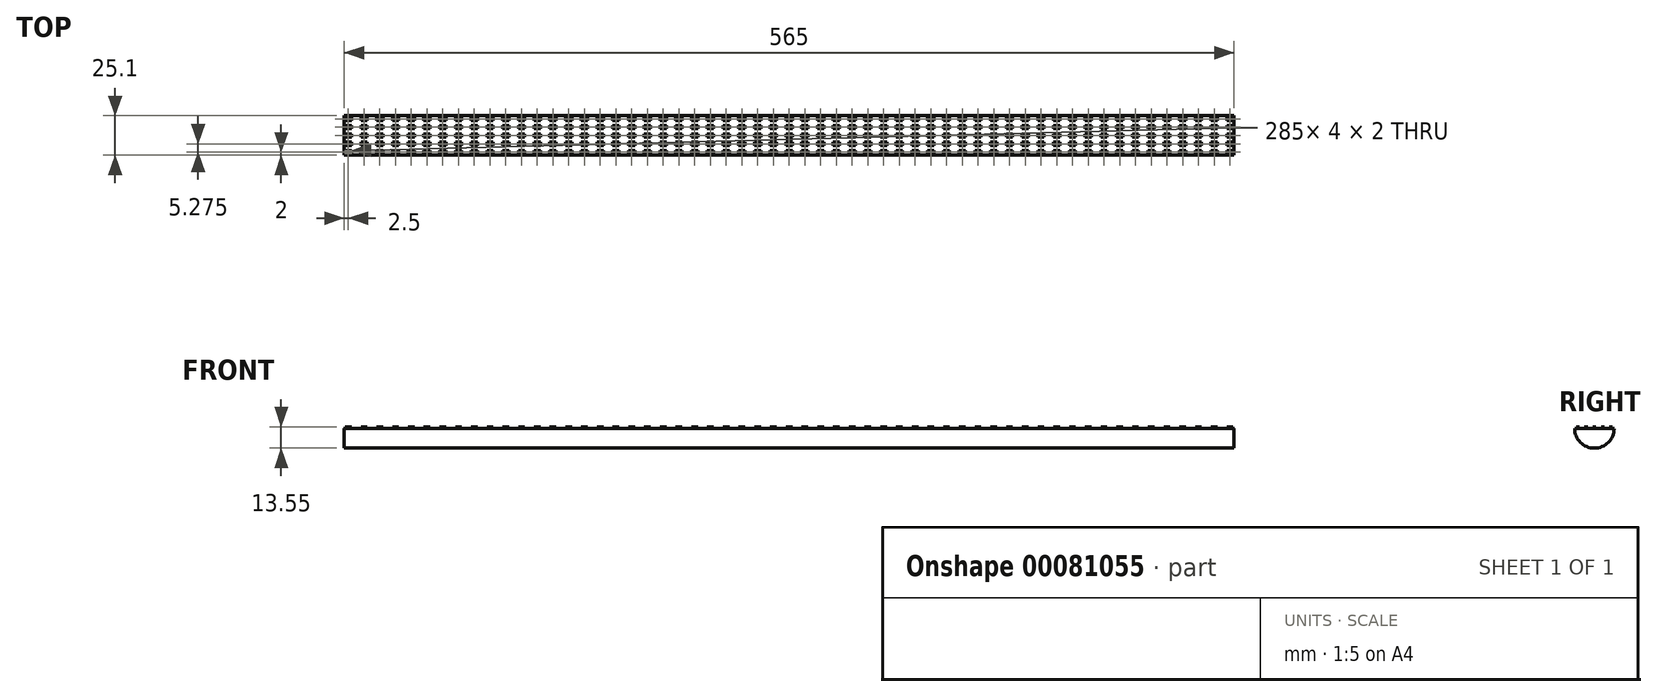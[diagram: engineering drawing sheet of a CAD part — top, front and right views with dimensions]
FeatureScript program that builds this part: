
annotation { "Feature Type Name" : "Feature", "Feature Type Description" : "" }
export const myFeature = defineFeature(function(context is Context, id is Id, definition is map)
    precondition{}
    {
        {
            var Q0;
            Q0=qCreatedBy(makeId("Right.planeOp"),FACE);
            var sketch = newSketch(context, id + "F0", { "sketchPlane" : qUnion([Q0])});
            skArc(sketch, "E0", {"start": v(-12.55, 0) * mm, "mid": v(0, -12.55) * mm, "end": v(12.55, 0) * mm});
            skLineSegment(sketch, "E1", {"start": v(-12.55, 0) * mm, "end": v(12.55, 0) * mm});
            skSolve(sketch);
        }
        {
            var Q0;
            Q0=qSketchRegion(id+"F0",true);
            extrude(context, id + "F1", {"entities" : qUnion([Q0]), "endBound" : BoundingType.SYMMETRIC, "depth" : 565 * mm});
        }
        {
            var Q0;
            Q0=makeQuery(id+"F1.opExtrude","SWEPT_FACE",FACE,{"disambiguationData":[OSD([sQuery(id+"F0.wireOp",EDGE,"E1")])]});
            var sketch = newSketch(context, id + "F2", { "sketchPlane" : qUnion([Q0])});
            skLineSegment(sketch, "E2.bottom", {"start": v(-282, 11.55) * mm, "end": v(-278, 11.55) * mm});
            skLineSegment(sketch, "E2.top", {"start": v(-282, 9.55) * mm, "end": v(-278, 9.55) * mm});
            skLineSegment(sketch, "E2.left", {"start": v(-282, 11.55) * mm, "end": v(-282, 9.55) * mm});
            skLineSegment(sketch, "E2.right", {"start": v(-278, 11.55) * mm, "end": v(-278, 9.55) * mm});
            skLineSegment(sketch, "E3.1.0.0", {"start": v(-282, 6.27) * mm, "end": v(-282, 4.27) * mm});
            skLineSegment(sketch, "E3.1.0.1", {"start": v(-282, 6.27) * mm, "end": v(-278, 6.27) * mm});
            skLineSegment(sketch, "E3.1.0.2", {"start": v(-278, 6.27) * mm, "end": v(-278, 4.27) * mm});
            skLineSegment(sketch, "E3.1.0.3", {"start": v(-282, 4.27) * mm, "end": v(-278, 4.27) * mm});
            skLineSegment(sketch, "E3.2.0.0", {"start": v(-282, 1) * mm, "end": v(-282, -1) * mm});
            skLineSegment(sketch, "E3.2.0.1", {"start": v(-282, 1) * mm, "end": v(-278, 1) * mm});
            skLineSegment(sketch, "E3.2.0.2", {"start": v(-278, 1) * mm, "end": v(-278, -1) * mm});
            skLineSegment(sketch, "E3.2.0.3", {"start": v(-282, -1) * mm, "end": v(-278, -1) * mm});
            skLineSegment(sketch, "E3.direction1", {"start": v(-278, 9.55) * mm, "end": v(-278, 4.27) * mm, "construction": true});
            skLineSegment(sketch, "E4.0.3.0", {"start": v(-282, -4.28) * mm, "end": v(-282, -6.28) * mm});
            skLineSegment(sketch, "E4.3.3.0", {"start": v(-282, -4.28) * mm, "end": v(-278, -4.28) * mm});
            skLineSegment(sketch, "E4.6.3.0", {"start": v(-278, -4.28) * mm, "end": v(-278, -6.28) * mm});
            skLineSegment(sketch, "E4.9.3.0", {"start": v(-282, -6.28) * mm, "end": v(-278, -6.28) * mm});
            skLineSegment(sketch, "E5.0.4.0", {"start": v(-282, -9.55) * mm, "end": v(-282, -11.55) * mm});
            skLineSegment(sketch, "E5.3.4.0", {"start": v(-282, -9.55) * mm, "end": v(-278, -9.55) * mm});
            skLineSegment(sketch, "E5.6.4.0", {"start": v(-278, -9.55) * mm, "end": v(-278, -11.55) * mm});
            skLineSegment(sketch, "E5.9.4.0", {"start": v(-282, -11.55) * mm, "end": v(-278, -11.55) * mm});
            skLineSegment(sketch, "E6.1.0.0", {"start": v(-272, -9.55) * mm, "end": v(-272, -11.55) * mm});
            skLineSegment(sketch, "E6.1.0.1", {"start": v(-268, -9.55) * mm, "end": v(-268, -11.55) * mm});
            skLineSegment(sketch, "E6.1.0.2", {"start": v(-272, -9.55) * mm, "end": v(-268, -9.55) * mm});
            skLineSegment(sketch, "E6.1.0.3", {"start": v(-268, 9.55) * mm, "end": v(-268, 4.27) * mm, "construction": true});
            skLineSegment(sketch, "E6.1.0.4", {"start": v(-272, -1) * mm, "end": v(-268, -1) * mm});
            skLineSegment(sketch, "E6.1.0.5", {"start": v(-272, -11.55) * mm, "end": v(-268, -11.55) * mm});
            skLineSegment(sketch, "E6.1.0.6", {"start": v(-268, 1) * mm, "end": v(-268, -1) * mm});
            skLineSegment(sketch, "E6.1.0.7", {"start": v(-272, 1) * mm, "end": v(-268, 1) * mm});
            skLineSegment(sketch, "E6.1.0.8", {"start": v(-272, 1) * mm, "end": v(-272, -1) * mm});
            skLineSegment(sketch, "E6.1.0.9", {"start": v(-272, 4.27) * mm, "end": v(-268, 4.27) * mm});
            skLineSegment(sketch, "E6.1.0.10", {"start": v(-268, 6.27) * mm, "end": v(-268, 4.27) * mm});
            skLineSegment(sketch, "E6.1.0.11", {"start": v(-272, 6.27) * mm, "end": v(-268, 6.27) * mm});
            skLineSegment(sketch, "E6.1.0.12", {"start": v(-272, 6.27) * mm, "end": v(-272, 4.27) * mm});
            skLineSegment(sketch, "E6.1.0.13", {"start": v(-268, 11.55) * mm, "end": v(-268, 9.55) * mm});
            skLineSegment(sketch, "E6.1.0.14", {"start": v(-272, 11.55) * mm, "end": v(-272, 9.55) * mm});
            skLineSegment(sketch, "E6.1.0.15", {"start": v(-272, 9.55) * mm, "end": v(-268, 9.55) * mm});
            skLineSegment(sketch, "E6.1.0.16", {"start": v(-272, -6.28) * mm, "end": v(-268, -6.28) * mm});
            skLineSegment(sketch, "E6.1.0.17", {"start": v(-272, 11.55) * mm, "end": v(-268, 11.55) * mm});
            skLineSegment(sketch, "E6.1.0.18", {"start": v(-268, -4.28) * mm, "end": v(-268, -6.28) * mm});
            skLineSegment(sketch, "E6.1.0.19", {"start": v(-272, -4.28) * mm, "end": v(-268, -4.28) * mm});
            skLineSegment(sketch, "E6.1.0.20", {"start": v(-272, -4.28) * mm, "end": v(-272, -6.28) * mm});
            skLineSegment(sketch, "E6.2.0.0", {"start": v(-262, -9.55) * mm, "end": v(-262, -11.55) * mm});
            skLineSegment(sketch, "E6.2.0.1", {"start": v(-258, -9.55) * mm, "end": v(-258, -11.55) * mm});
            skLineSegment(sketch, "E6.2.0.2", {"start": v(-262, -9.55) * mm, "end": v(-258, -9.55) * mm});
            skLineSegment(sketch, "E6.2.0.3", {"start": v(-258, 9.55) * mm, "end": v(-258, 4.27) * mm, "construction": true});
            skLineSegment(sketch, "E6.2.0.4", {"start": v(-262, -1) * mm, "end": v(-258, -1) * mm});
            skLineSegment(sketch, "E6.2.0.5", {"start": v(-262, -11.55) * mm, "end": v(-258, -11.55) * mm});
            skLineSegment(sketch, "E6.2.0.6", {"start": v(-258, 1) * mm, "end": v(-258, -1) * mm});
            skLineSegment(sketch, "E6.2.0.7", {"start": v(-262, 1) * mm, "end": v(-258, 1) * mm});
            skLineSegment(sketch, "E6.2.0.8", {"start": v(-262, 1) * mm, "end": v(-262, -1) * mm});
            skLineSegment(sketch, "E6.2.0.9", {"start": v(-262, 4.27) * mm, "end": v(-258, 4.27) * mm});
            skLineSegment(sketch, "E6.2.0.10", {"start": v(-258, 6.27) * mm, "end": v(-258, 4.27) * mm});
            skLineSegment(sketch, "E6.2.0.11", {"start": v(-262, 6.27) * mm, "end": v(-258, 6.27) * mm});
            skLineSegment(sketch, "E6.2.0.12", {"start": v(-262, 6.27) * mm, "end": v(-262, 4.27) * mm});
            skLineSegment(sketch, "E6.2.0.13", {"start": v(-258, 11.55) * mm, "end": v(-258, 9.55) * mm});
            skLineSegment(sketch, "E6.2.0.14", {"start": v(-262, 11.55) * mm, "end": v(-262, 9.55) * mm});
            skLineSegment(sketch, "E6.2.0.15", {"start": v(-262, 9.55) * mm, "end": v(-258, 9.55) * mm});
            skLineSegment(sketch, "E6.2.0.16", {"start": v(-262, -6.28) * mm, "end": v(-258, -6.28) * mm});
            skLineSegment(sketch, "E6.2.0.17", {"start": v(-262, 11.55) * mm, "end": v(-258, 11.55) * mm});
            skLineSegment(sketch, "E6.2.0.18", {"start": v(-258, -4.28) * mm, "end": v(-258, -6.28) * mm});
            skLineSegment(sketch, "E6.2.0.19", {"start": v(-262, -4.28) * mm, "end": v(-258, -4.28) * mm});
            skLineSegment(sketch, "E6.2.0.20", {"start": v(-262, -4.28) * mm, "end": v(-262, -6.28) * mm});
            skLineSegment(sketch, "E6.3.0.0", {"start": v(-252, -9.55) * mm, "end": v(-252, -11.55) * mm});
            skLineSegment(sketch, "E6.3.0.1", {"start": v(-248, -9.55) * mm, "end": v(-248, -11.55) * mm});
            skLineSegment(sketch, "E6.3.0.2", {"start": v(-252, -9.55) * mm, "end": v(-248, -9.55) * mm});
            skLineSegment(sketch, "E6.3.0.3", {"start": v(-248, 9.55) * mm, "end": v(-248, 4.27) * mm, "construction": true});
            skLineSegment(sketch, "E6.3.0.4", {"start": v(-252, -1) * mm, "end": v(-248, -1) * mm});
            skLineSegment(sketch, "E6.3.0.5", {"start": v(-252, -11.55) * mm, "end": v(-248, -11.55) * mm});
            skLineSegment(sketch, "E6.3.0.6", {"start": v(-248, 1) * mm, "end": v(-248, -1) * mm});
            skLineSegment(sketch, "E6.3.0.7", {"start": v(-252, 1) * mm, "end": v(-248, 1) * mm});
            skLineSegment(sketch, "E6.3.0.8", {"start": v(-252, 1) * mm, "end": v(-252, -1) * mm});
            skLineSegment(sketch, "E6.3.0.9", {"start": v(-252, 4.27) * mm, "end": v(-248, 4.27) * mm});
            skLineSegment(sketch, "E6.3.0.10", {"start": v(-248, 6.27) * mm, "end": v(-248, 4.27) * mm});
            skLineSegment(sketch, "E6.3.0.11", {"start": v(-252, 6.27) * mm, "end": v(-248, 6.27) * mm});
            skLineSegment(sketch, "E6.3.0.12", {"start": v(-252, 6.27) * mm, "end": v(-252, 4.27) * mm});
            skLineSegment(sketch, "E6.3.0.13", {"start": v(-248, 11.55) * mm, "end": v(-248, 9.55) * mm});
            skLineSegment(sketch, "E6.3.0.14", {"start": v(-252, 11.55) * mm, "end": v(-252, 9.55) * mm});
            skLineSegment(sketch, "E6.3.0.15", {"start": v(-252, 9.55) * mm, "end": v(-248, 9.55) * mm});
            skLineSegment(sketch, "E6.3.0.16", {"start": v(-252, -6.28) * mm, "end": v(-248, -6.28) * mm});
            skLineSegment(sketch, "E6.3.0.17", {"start": v(-252, 11.55) * mm, "end": v(-248, 11.55) * mm});
            skLineSegment(sketch, "E6.3.0.18", {"start": v(-248, -4.28) * mm, "end": v(-248, -6.28) * mm});
            skLineSegment(sketch, "E6.3.0.19", {"start": v(-252, -4.28) * mm, "end": v(-248, -4.28) * mm});
            skLineSegment(sketch, "E6.3.0.20", {"start": v(-252, -4.28) * mm, "end": v(-252, -6.28) * mm});
            skLineSegment(sketch, "E6.4.0.0", {"start": v(-242, -9.55) * mm, "end": v(-242, -11.55) * mm});
            skLineSegment(sketch, "E6.4.0.1", {"start": v(-238, -9.55) * mm, "end": v(-238, -11.55) * mm});
            skLineSegment(sketch, "E6.4.0.2", {"start": v(-242, -9.55) * mm, "end": v(-238, -9.55) * mm});
            skLineSegment(sketch, "E6.4.0.3", {"start": v(-238, 9.55) * mm, "end": v(-238, 4.27) * mm, "construction": true});
            skLineSegment(sketch, "E6.4.0.4", {"start": v(-242, -1) * mm, "end": v(-238, -1) * mm});
            skLineSegment(sketch, "E6.4.0.5", {"start": v(-242, -11.55) * mm, "end": v(-238, -11.55) * mm});
            skLineSegment(sketch, "E6.4.0.6", {"start": v(-238, 1) * mm, "end": v(-238, -1) * mm});
            skLineSegment(sketch, "E6.4.0.7", {"start": v(-242, 1) * mm, "end": v(-238, 1) * mm});
            skLineSegment(sketch, "E6.4.0.8", {"start": v(-242, 1) * mm, "end": v(-242, -1) * mm});
            skLineSegment(sketch, "E6.4.0.9", {"start": v(-242, 4.27) * mm, "end": v(-238, 4.27) * mm});
            skLineSegment(sketch, "E6.4.0.10", {"start": v(-238, 6.27) * mm, "end": v(-238, 4.27) * mm});
            skLineSegment(sketch, "E6.4.0.11", {"start": v(-242, 6.27) * mm, "end": v(-238, 6.27) * mm});
            skLineSegment(sketch, "E6.4.0.12", {"start": v(-242, 6.27) * mm, "end": v(-242, 4.27) * mm});
            skLineSegment(sketch, "E6.4.0.13", {"start": v(-238, 11.55) * mm, "end": v(-238, 9.55) * mm});
            skLineSegment(sketch, "E6.4.0.14", {"start": v(-242, 11.55) * mm, "end": v(-242, 9.55) * mm});
            skLineSegment(sketch, "E6.4.0.15", {"start": v(-242, 9.55) * mm, "end": v(-238, 9.55) * mm});
            skLineSegment(sketch, "E6.4.0.16", {"start": v(-242, -6.28) * mm, "end": v(-238, -6.28) * mm});
            skLineSegment(sketch, "E6.4.0.17", {"start": v(-242, 11.55) * mm, "end": v(-238, 11.55) * mm});
            skLineSegment(sketch, "E6.4.0.18", {"start": v(-238, -4.28) * mm, "end": v(-238, -6.28) * mm});
            skLineSegment(sketch, "E6.4.0.19", {"start": v(-242, -4.28) * mm, "end": v(-238, -4.28) * mm});
            skLineSegment(sketch, "E6.4.0.20", {"start": v(-242, -4.28) * mm, "end": v(-242, -6.28) * mm});
            skLineSegment(sketch, "E6.5.0.0", {"start": v(-232, -9.55) * mm, "end": v(-232, -11.55) * mm});
            skLineSegment(sketch, "E6.5.0.1", {"start": v(-228, -9.55) * mm, "end": v(-228, -11.55) * mm});
            skLineSegment(sketch, "E6.5.0.2", {"start": v(-232, -9.55) * mm, "end": v(-228, -9.55) * mm});
            skLineSegment(sketch, "E6.5.0.3", {"start": v(-228, 9.55) * mm, "end": v(-228, 4.27) * mm, "construction": true});
            skLineSegment(sketch, "E6.5.0.4", {"start": v(-232, -1) * mm, "end": v(-228, -1) * mm});
            skLineSegment(sketch, "E6.5.0.5", {"start": v(-232, -11.55) * mm, "end": v(-228, -11.55) * mm});
            skLineSegment(sketch, "E6.5.0.6", {"start": v(-228, 1) * mm, "end": v(-228, -1) * mm});
            skLineSegment(sketch, "E6.5.0.7", {"start": v(-232, 1) * mm, "end": v(-228, 1) * mm});
            skLineSegment(sketch, "E6.5.0.8", {"start": v(-232, 1) * mm, "end": v(-232, -1) * mm});
            skLineSegment(sketch, "E6.5.0.9", {"start": v(-232, 4.27) * mm, "end": v(-228, 4.27) * mm});
            skLineSegment(sketch, "E6.5.0.10", {"start": v(-228, 6.27) * mm, "end": v(-228, 4.27) * mm});
            skLineSegment(sketch, "E6.5.0.11", {"start": v(-232, 6.27) * mm, "end": v(-228, 6.27) * mm});
            skLineSegment(sketch, "E6.5.0.12", {"start": v(-232, 6.27) * mm, "end": v(-232, 4.27) * mm});
            skLineSegment(sketch, "E6.5.0.13", {"start": v(-228, 11.55) * mm, "end": v(-228, 9.55) * mm});
            skLineSegment(sketch, "E6.5.0.14", {"start": v(-232, 11.55) * mm, "end": v(-232, 9.55) * mm});
            skLineSegment(sketch, "E6.5.0.15", {"start": v(-232, 9.55) * mm, "end": v(-228, 9.55) * mm});
            skLineSegment(sketch, "E6.5.0.16", {"start": v(-232, -6.28) * mm, "end": v(-228, -6.28) * mm});
            skLineSegment(sketch, "E6.5.0.17", {"start": v(-232, 11.55) * mm, "end": v(-228, 11.55) * mm});
            skLineSegment(sketch, "E6.5.0.18", {"start": v(-228, -4.28) * mm, "end": v(-228, -6.28) * mm});
            skLineSegment(sketch, "E6.5.0.19", {"start": v(-232, -4.28) * mm, "end": v(-228, -4.28) * mm});
            skLineSegment(sketch, "E6.5.0.20", {"start": v(-232, -4.28) * mm, "end": v(-232, -6.28) * mm});
            skLineSegment(sketch, "E6.6.0.0", {"start": v(-222, -9.55) * mm, "end": v(-222, -11.55) * mm});
            skLineSegment(sketch, "E6.6.0.1", {"start": v(-218, -9.55) * mm, "end": v(-218, -11.55) * mm});
            skLineSegment(sketch, "E6.6.0.2", {"start": v(-222, -9.55) * mm, "end": v(-218, -9.55) * mm});
            skLineSegment(sketch, "E6.6.0.3", {"start": v(-218, 9.55) * mm, "end": v(-218, 4.27) * mm, "construction": true});
            skLineSegment(sketch, "E6.6.0.4", {"start": v(-222, -1) * mm, "end": v(-218, -1) * mm});
            skLineSegment(sketch, "E6.6.0.5", {"start": v(-222, -11.55) * mm, "end": v(-218, -11.55) * mm});
            skLineSegment(sketch, "E6.6.0.6", {"start": v(-218, 1) * mm, "end": v(-218, -1) * mm});
            skLineSegment(sketch, "E6.6.0.7", {"start": v(-222, 1) * mm, "end": v(-218, 1) * mm});
            skLineSegment(sketch, "E6.6.0.8", {"start": v(-222, 1) * mm, "end": v(-222, -1) * mm});
            skLineSegment(sketch, "E6.6.0.9", {"start": v(-222, 4.27) * mm, "end": v(-218, 4.27) * mm});
            skLineSegment(sketch, "E6.6.0.10", {"start": v(-218, 6.27) * mm, "end": v(-218, 4.27) * mm});
            skLineSegment(sketch, "E6.6.0.11", {"start": v(-222, 6.27) * mm, "end": v(-218, 6.27) * mm});
            skLineSegment(sketch, "E6.6.0.12", {"start": v(-222, 6.27) * mm, "end": v(-222, 4.27) * mm});
            skLineSegment(sketch, "E6.6.0.13", {"start": v(-218, 11.55) * mm, "end": v(-218, 9.55) * mm});
            skLineSegment(sketch, "E6.6.0.14", {"start": v(-222, 11.55) * mm, "end": v(-222, 9.55) * mm});
            skLineSegment(sketch, "E6.6.0.15", {"start": v(-222, 9.55) * mm, "end": v(-218, 9.55) * mm});
            skLineSegment(sketch, "E6.6.0.16", {"start": v(-222, -6.28) * mm, "end": v(-218, -6.28) * mm});
            skLineSegment(sketch, "E6.6.0.17", {"start": v(-222, 11.55) * mm, "end": v(-218, 11.55) * mm});
            skLineSegment(sketch, "E6.6.0.18", {"start": v(-218, -4.28) * mm, "end": v(-218, -6.28) * mm});
            skLineSegment(sketch, "E6.6.0.19", {"start": v(-222, -4.28) * mm, "end": v(-218, -4.28) * mm});
            skLineSegment(sketch, "E6.6.0.20", {"start": v(-222, -4.28) * mm, "end": v(-222, -6.28) * mm});
            skLineSegment(sketch, "E6.7.0.0", {"start": v(-212, -9.55) * mm, "end": v(-212, -11.55) * mm});
            skLineSegment(sketch, "E6.7.0.1", {"start": v(-208, -9.55) * mm, "end": v(-208, -11.55) * mm});
            skLineSegment(sketch, "E6.7.0.2", {"start": v(-212, -9.55) * mm, "end": v(-208, -9.55) * mm});
            skLineSegment(sketch, "E6.7.0.3", {"start": v(-208, 9.55) * mm, "end": v(-208, 4.27) * mm, "construction": true});
            skLineSegment(sketch, "E6.7.0.4", {"start": v(-212, -1) * mm, "end": v(-208, -1) * mm});
            skLineSegment(sketch, "E6.7.0.5", {"start": v(-212, -11.55) * mm, "end": v(-208, -11.55) * mm});
            skLineSegment(sketch, "E6.7.0.6", {"start": v(-208, 1) * mm, "end": v(-208, -1) * mm});
            skLineSegment(sketch, "E6.7.0.7", {"start": v(-212, 1) * mm, "end": v(-208, 1) * mm});
            skLineSegment(sketch, "E6.7.0.8", {"start": v(-212, 1) * mm, "end": v(-212, -1) * mm});
            skLineSegment(sketch, "E6.7.0.9", {"start": v(-212, 4.27) * mm, "end": v(-208, 4.27) * mm});
            skLineSegment(sketch, "E6.7.0.10", {"start": v(-208, 6.27) * mm, "end": v(-208, 4.27) * mm});
            skLineSegment(sketch, "E6.7.0.11", {"start": v(-212, 6.27) * mm, "end": v(-208, 6.27) * mm});
            skLineSegment(sketch, "E6.7.0.12", {"start": v(-212, 6.27) * mm, "end": v(-212, 4.27) * mm});
            skLineSegment(sketch, "E6.7.0.13", {"start": v(-208, 11.55) * mm, "end": v(-208, 9.55) * mm});
            skLineSegment(sketch, "E6.7.0.14", {"start": v(-212, 11.55) * mm, "end": v(-212, 9.55) * mm});
            skLineSegment(sketch, "E6.7.0.15", {"start": v(-212, 9.55) * mm, "end": v(-208, 9.55) * mm});
            skLineSegment(sketch, "E6.7.0.16", {"start": v(-212, -6.28) * mm, "end": v(-208, -6.28) * mm});
            skLineSegment(sketch, "E6.7.0.17", {"start": v(-212, 11.55) * mm, "end": v(-208, 11.55) * mm});
            skLineSegment(sketch, "E6.7.0.18", {"start": v(-208, -4.28) * mm, "end": v(-208, -6.28) * mm});
            skLineSegment(sketch, "E6.7.0.19", {"start": v(-212, -4.28) * mm, "end": v(-208, -4.28) * mm});
            skLineSegment(sketch, "E6.7.0.20", {"start": v(-212, -4.28) * mm, "end": v(-212, -6.28) * mm});
            skLineSegment(sketch, "E6.8.0.0", {"start": v(-202, -9.55) * mm, "end": v(-202, -11.55) * mm});
            skLineSegment(sketch, "E6.8.0.1", {"start": v(-198, -9.55) * mm, "end": v(-198, -11.55) * mm});
            skLineSegment(sketch, "E6.8.0.2", {"start": v(-202, -9.55) * mm, "end": v(-198, -9.55) * mm});
            skLineSegment(sketch, "E6.8.0.3", {"start": v(-198, 9.55) * mm, "end": v(-198, 4.27) * mm, "construction": true});
            skLineSegment(sketch, "E6.8.0.4", {"start": v(-202, -1) * mm, "end": v(-198, -1) * mm});
            skLineSegment(sketch, "E6.8.0.5", {"start": v(-202, -11.55) * mm, "end": v(-198, -11.55) * mm});
            skLineSegment(sketch, "E6.8.0.6", {"start": v(-198, 1) * mm, "end": v(-198, -1) * mm});
            skLineSegment(sketch, "E6.8.0.7", {"start": v(-202, 1) * mm, "end": v(-198, 1) * mm});
            skLineSegment(sketch, "E6.8.0.8", {"start": v(-202, 1) * mm, "end": v(-202, -1) * mm});
            skLineSegment(sketch, "E6.8.0.9", {"start": v(-202, 4.27) * mm, "end": v(-198, 4.27) * mm});
            skLineSegment(sketch, "E6.8.0.10", {"start": v(-198, 6.27) * mm, "end": v(-198, 4.27) * mm});
            skLineSegment(sketch, "E6.8.0.11", {"start": v(-202, 6.27) * mm, "end": v(-198, 6.27) * mm});
            skLineSegment(sketch, "E6.8.0.12", {"start": v(-202, 6.27) * mm, "end": v(-202, 4.27) * mm});
            skLineSegment(sketch, "E6.8.0.13", {"start": v(-198, 11.55) * mm, "end": v(-198, 9.55) * mm});
            skLineSegment(sketch, "E6.8.0.14", {"start": v(-202, 11.55) * mm, "end": v(-202, 9.55) * mm});
            skLineSegment(sketch, "E6.8.0.15", {"start": v(-202, 9.55) * mm, "end": v(-198, 9.55) * mm});
            skLineSegment(sketch, "E6.8.0.16", {"start": v(-202, -6.28) * mm, "end": v(-198, -6.28) * mm});
            skLineSegment(sketch, "E6.8.0.17", {"start": v(-202, 11.55) * mm, "end": v(-198, 11.55) * mm});
            skLineSegment(sketch, "E6.8.0.18", {"start": v(-198, -4.28) * mm, "end": v(-198, -6.28) * mm});
            skLineSegment(sketch, "E6.8.0.19", {"start": v(-202, -4.28) * mm, "end": v(-198, -4.28) * mm});
            skLineSegment(sketch, "E6.8.0.20", {"start": v(-202, -4.28) * mm, "end": v(-202, -6.28) * mm});
            skLineSegment(sketch, "E6.9.0.0", {"start": v(-192, -9.55) * mm, "end": v(-192, -11.55) * mm});
            skLineSegment(sketch, "E6.9.0.1", {"start": v(-188, -9.55) * mm, "end": v(-188, -11.55) * mm});
            skLineSegment(sketch, "E6.9.0.2", {"start": v(-192, -9.55) * mm, "end": v(-188, -9.55) * mm});
            skLineSegment(sketch, "E6.9.0.3", {"start": v(-188, 9.55) * mm, "end": v(-188, 4.27) * mm, "construction": true});
            skLineSegment(sketch, "E6.9.0.4", {"start": v(-192, -1) * mm, "end": v(-188, -1) * mm});
            skLineSegment(sketch, "E6.9.0.5", {"start": v(-192, -11.55) * mm, "end": v(-188, -11.55) * mm});
            skLineSegment(sketch, "E6.9.0.6", {"start": v(-188, 1) * mm, "end": v(-188, -1) * mm});
            skLineSegment(sketch, "E6.9.0.7", {"start": v(-192, 1) * mm, "end": v(-188, 1) * mm});
            skLineSegment(sketch, "E6.9.0.8", {"start": v(-192, 1) * mm, "end": v(-192, -1) * mm});
            skLineSegment(sketch, "E6.9.0.9", {"start": v(-192, 4.27) * mm, "end": v(-188, 4.27) * mm});
            skLineSegment(sketch, "E6.9.0.10", {"start": v(-188, 6.27) * mm, "end": v(-188, 4.27) * mm});
            skLineSegment(sketch, "E6.9.0.11", {"start": v(-192, 6.27) * mm, "end": v(-188, 6.27) * mm});
            skLineSegment(sketch, "E6.9.0.12", {"start": v(-192, 6.27) * mm, "end": v(-192, 4.27) * mm});
            skLineSegment(sketch, "E6.9.0.13", {"start": v(-188, 11.55) * mm, "end": v(-188, 9.55) * mm});
            skLineSegment(sketch, "E6.9.0.14", {"start": v(-192, 11.55) * mm, "end": v(-192, 9.55) * mm});
            skLineSegment(sketch, "E6.9.0.15", {"start": v(-192, 9.55) * mm, "end": v(-188, 9.55) * mm});
            skLineSegment(sketch, "E6.9.0.16", {"start": v(-192, -6.28) * mm, "end": v(-188, -6.28) * mm});
            skLineSegment(sketch, "E6.9.0.17", {"start": v(-192, 11.55) * mm, "end": v(-188, 11.55) * mm});
            skLineSegment(sketch, "E6.9.0.18", {"start": v(-188, -4.28) * mm, "end": v(-188, -6.28) * mm});
            skLineSegment(sketch, "E6.9.0.19", {"start": v(-192, -4.28) * mm, "end": v(-188, -4.28) * mm});
            skLineSegment(sketch, "E6.9.0.20", {"start": v(-192, -4.28) * mm, "end": v(-192, -6.28) * mm});
            skLineSegment(sketch, "E6.direction1", {"start": v(-282, -11.55) * mm, "end": v(-272, -11.55) * mm, "construction": true});
            skLineSegment(sketch, "E7.1.0.0", {"start": v(-172, -9.55) * mm, "end": v(-168, -9.55) * mm});
            skLineSegment(sketch, "E7.1.0.1", {"start": v(-168, -9.55) * mm, "end": v(-168, -11.55) * mm});
            skLineSegment(sketch, "E7.1.0.2", {"start": v(-102, 11.55) * mm, "end": v(-102, 9.55) * mm});
            skLineSegment(sketch, "E7.1.0.3", {"start": v(-112, -1) * mm, "end": v(-108, -1) * mm});
            skLineSegment(sketch, "E7.1.0.4", {"start": v(-132, 11.55) * mm, "end": v(-132, 9.55) * mm});
            skLineSegment(sketch, "E7.1.0.5", {"start": v(-102, 9.55) * mm, "end": v(-98, 9.55) * mm});
            skLineSegment(sketch, "E7.1.0.6", {"start": v(-162, 11.55) * mm, "end": v(-162, 9.55) * mm});
            skLineSegment(sketch, "E7.1.0.7", {"start": v(-132, 9.55) * mm, "end": v(-128, 9.55) * mm});
            skLineSegment(sketch, "E7.1.0.8", {"start": v(-102, -9.55) * mm, "end": v(-102, -11.55) * mm});
            skLineSegment(sketch, "E7.1.0.9", {"start": v(-162, 9.55) * mm, "end": v(-158, 9.55) * mm});
            skLineSegment(sketch, "E7.1.0.10", {"start": v(-108, 1) * mm, "end": v(-108, -1) * mm});
            skLineSegment(sketch, "E7.1.0.11", {"start": v(-92, 6.27) * mm, "end": v(-92, 4.27) * mm});
            skLineSegment(sketch, "E7.1.0.12", {"start": v(-102, 11.55) * mm, "end": v(-98, 11.55) * mm});
            skLineSegment(sketch, "E7.1.0.13", {"start": v(-98, -9.55) * mm, "end": v(-98, -11.55) * mm});
            skLineSegment(sketch, "E7.1.0.14", {"start": v(-172, -11.55) * mm, "end": v(-168, -11.55) * mm});
            skLineSegment(sketch, "E7.1.0.15", {"start": v(-112, 1) * mm, "end": v(-108, 1) * mm});
            skLineSegment(sketch, "E7.1.0.16", {"start": v(-132, 11.55) * mm, "end": v(-128, 11.55) * mm});
            skLineSegment(sketch, "E7.1.0.17", {"start": v(-128, -9.55) * mm, "end": v(-128, -11.55) * mm});
            skLineSegment(sketch, "E7.1.0.18", {"start": v(-102, -9.55) * mm, "end": v(-98, -9.55) * mm});
            skLineSegment(sketch, "E7.1.0.19", {"start": v(-162, 11.55) * mm, "end": v(-158, 11.55) * mm});
            skLineSegment(sketch, "E7.1.0.20", {"start": v(-132, -9.55) * mm, "end": v(-128, -9.55) * mm});
            skLineSegment(sketch, "E7.1.0.21", {"start": v(-132, -1) * mm, "end": v(-128, -1) * mm});
            skLineSegment(sketch, "E7.1.0.22", {"start": v(-102, -11.55) * mm, "end": v(-98, -11.55) * mm});
            skLineSegment(sketch, "E7.1.0.23", {"start": v(-162, -1) * mm, "end": v(-158, -1) * mm});
            skLineSegment(sketch, "E7.1.0.24", {"start": v(-132, -11.55) * mm, "end": v(-128, -11.55) * mm});
            skLineSegment(sketch, "E7.1.0.25", {"start": v(-122, -9.55) * mm, "end": v(-122, -11.55) * mm});
            skLineSegment(sketch, "E7.1.0.26", {"start": v(-88, -9.55) * mm, "end": v(-88, -11.55) * mm});
            skLineSegment(sketch, "E7.1.0.27", {"start": v(-128, 1) * mm, "end": v(-128, -1) * mm});
            skLineSegment(sketch, "E7.1.0.28", {"start": v(-152, -9.55) * mm, "end": v(-152, -11.55) * mm});
            skLineSegment(sketch, "E7.1.0.29", {"start": v(-118, -9.55) * mm, "end": v(-118, -11.55) * mm});
            skLineSegment(sketch, "E7.1.0.30", {"start": v(-92, -9.55) * mm, "end": v(-88, -9.55) * mm});
            skLineSegment(sketch, "E7.1.0.31", {"start": v(-132, 1) * mm, "end": v(-128, 1) * mm});
            skLineSegment(sketch, "E7.1.0.32", {"start": v(-148, -9.55) * mm, "end": v(-148, -11.55) * mm});
            skLineSegment(sketch, "E7.1.0.33", {"start": v(-122, -9.55) * mm, "end": v(-118, -9.55) * mm});
            skLineSegment(sketch, "E7.1.0.34", {"start": v(-152, -9.55) * mm, "end": v(-148, -9.55) * mm});
            skLineSegment(sketch, "E7.1.0.35", {"start": v(-112, 11.55) * mm, "end": v(-112, 9.55) * mm});
            skLineSegment(sketch, "E7.1.0.36", {"start": v(-172, 6.27) * mm, "end": v(-172, 4.27) * mm});
            skLineSegment(sketch, "E7.1.0.37", {"start": v(-112, 9.55) * mm, "end": v(-108, 9.55) * mm});
            skLineSegment(sketch, "E7.1.0.38", {"start": v(-92, -11.55) * mm, "end": v(-88, -11.55) * mm});
            skLineSegment(sketch, "E7.1.0.39", {"start": v(-162, 1) * mm, "end": v(-162, -1) * mm});
            skLineSegment(sketch, "E7.1.0.40", {"start": v(-122, -11.55) * mm, "end": v(-118, -11.55) * mm});
            skLineSegment(sketch, "E7.1.0.41", {"start": v(-182, 11.55) * mm, "end": v(-178, 11.55) * mm});
            skLineSegment(sketch, "E7.1.0.42", {"start": v(-182, 9.55) * mm, "end": v(-178, 9.55) * mm});
            skLineSegment(sketch, "E7.1.0.43", {"start": v(-182, 11.55) * mm, "end": v(-182, 9.55) * mm});
            skLineSegment(sketch, "E7.1.0.44", {"start": v(-182, 6.27) * mm, "end": v(-182, 4.27) * mm});
            skLineSegment(sketch, "E7.1.0.45", {"start": v(-182, 6.27) * mm, "end": v(-178, 6.27) * mm});
            skLineSegment(sketch, "E7.1.0.46", {"start": v(-182, 4.27) * mm, "end": v(-178, 4.27) * mm});
            skLineSegment(sketch, "E7.1.0.47", {"start": v(-152, -11.55) * mm, "end": v(-148, -11.55) * mm});
            skLineSegment(sketch, "E7.1.0.48", {"start": v(-112, 11.55) * mm, "end": v(-108, 11.55) * mm});
            skLineSegment(sketch, "E7.1.0.49", {"start": v(-162, 6.27) * mm, "end": v(-162, 4.27) * mm});
            skLineSegment(sketch, "E7.1.0.50", {"start": v(-172, 11.55) * mm, "end": v(-168, 11.55) * mm});
            skLineSegment(sketch, "E7.1.0.51", {"start": v(-128, 11.55) * mm, "end": v(-128, 9.55) * mm});
            skLineSegment(sketch, "E7.1.0.52", {"start": v(-138, -4.28) * mm, "end": v(-138, -6.28) * mm});
            skLineSegment(sketch, "E7.1.0.53", {"start": v(-142, -9.55) * mm, "end": v(-138, -9.55) * mm});
            skLineSegment(sketch, "E7.1.0.54", {"start": v(-152, 1) * mm, "end": v(-148, 1) * mm});
            skLineSegment(sketch, "E7.1.0.55", {"start": v(-112, -4.28) * mm, "end": v(-108, -4.28) * mm});
            skLineSegment(sketch, "E7.1.0.56", {"start": v(-92, 4.27) * mm, "end": v(-88, 4.27) * mm});
            skLineSegment(sketch, "E7.1.0.57", {"start": v(-138, 9.55) * mm, "end": v(-138, 4.27) * mm, "construction": true});
            skLineSegment(sketch, "E7.1.0.58", {"start": v(-152, 1) * mm, "end": v(-152, -1) * mm});
            skLineSegment(sketch, "E7.1.0.59", {"start": v(-158, 11.55) * mm, "end": v(-158, 9.55) * mm});
            skLineSegment(sketch, "E7.1.0.60", {"start": v(-168, -4.28) * mm, "end": v(-168, -6.28) * mm});
            skLineSegment(sketch, "E7.1.0.61", {"start": v(-122, 4.27) * mm, "end": v(-118, 4.27) * mm});
            skLineSegment(sketch, "E7.1.0.62", {"start": v(-142, -4.28) * mm, "end": v(-138, -4.28) * mm});
            skLineSegment(sketch, "E7.1.0.63", {"start": v(-88, 6.27) * mm, "end": v(-88, 4.27) * mm});
            skLineSegment(sketch, "E7.1.0.64", {"start": v(-112, -4.28) * mm, "end": v(-112, -6.28) * mm});
            skLineSegment(sketch, "E7.1.0.65", {"start": v(-168, 9.55) * mm, "end": v(-168, 4.27) * mm, "construction": true});
            skLineSegment(sketch, "E7.1.0.66", {"start": v(-142, -1) * mm, "end": v(-138, -1) * mm});
            skLineSegment(sketch, "E7.1.0.67", {"start": v(-152, 4.27) * mm, "end": v(-148, 4.27) * mm});
            skLineSegment(sketch, "E7.1.0.68", {"start": v(-172, -4.28) * mm, "end": v(-168, -4.28) * mm});
            skLineSegment(sketch, "E7.1.0.69", {"start": v(-112, -11.55) * mm, "end": v(-108, -11.55) * mm});
            skLineSegment(sketch, "E7.1.0.70", {"start": v(-118, 6.27) * mm, "end": v(-118, 4.27) * mm});
            skLineSegment(sketch, "E7.1.0.71", {"start": v(-92, 6.27) * mm, "end": v(-88, 6.27) * mm});
            skLineSegment(sketch, "E7.1.0.72", {"start": v(-102, -6.28) * mm, "end": v(-98, -6.28) * mm});
            skLineSegment(sketch, "E7.1.0.73", {"start": v(-142, -11.55) * mm, "end": v(-138, -11.55) * mm});
            skLineSegment(sketch, "E7.1.0.74", {"start": v(-148, 6.27) * mm, "end": v(-148, 4.27) * mm});
            skLineSegment(sketch, "E7.1.0.75", {"start": v(-122, 6.27) * mm, "end": v(-118, 6.27) * mm});
            skLineSegment(sketch, "E7.1.0.76", {"start": v(-132, -6.28) * mm, "end": v(-128, -6.28) * mm});
            skLineSegment(sketch, "E7.1.0.77", {"start": v(-132, -9.55) * mm, "end": v(-132, -11.55) * mm});
            skLineSegment(sketch, "E7.1.0.78", {"start": v(-138, 1) * mm, "end": v(-138, -1) * mm});
            skLineSegment(sketch, "E7.1.0.79", {"start": v(-152, 6.27) * mm, "end": v(-148, 6.27) * mm});
            skLineSegment(sketch, "E7.1.0.80", {"start": v(-162, -6.28) * mm, "end": v(-158, -6.28) * mm});
            skLineSegment(sketch, "E7.1.0.81", {"start": v(-162, -9.55) * mm, "end": v(-162, -11.55) * mm});
            skLineSegment(sketch, "E7.1.0.82", {"start": v(-122, 6.27) * mm, "end": v(-122, 4.27) * mm});
            skLineSegment(sketch, "E7.1.0.83", {"start": v(-88, 11.55) * mm, "end": v(-88, 9.55) * mm});
            skLineSegment(sketch, "E7.1.0.84", {"start": v(-98, -4.28) * mm, "end": v(-98, -6.28) * mm});
            skLineSegment(sketch, "E7.1.0.85", {"start": v(-142, 1) * mm, "end": v(-138, 1) * mm});
            skLineSegment(sketch, "E7.1.0.86", {"start": v(-152, 6.27) * mm, "end": v(-152, 4.27) * mm});
            skLineSegment(sketch, "E7.1.0.87", {"start": v(-158, -9.55) * mm, "end": v(-158, -11.55) * mm});
            skLineSegment(sketch, "E7.1.0.88", {"start": v(-112, 1) * mm, "end": v(-112, -1) * mm});
            skLineSegment(sketch, "E7.1.0.89", {"start": v(-118, 11.55) * mm, "end": v(-118, 9.55) * mm});
            skLineSegment(sketch, "E7.1.0.90", {"start": v(-128, -4.28) * mm, "end": v(-128, -6.28) * mm});
            skLineSegment(sketch, "E7.1.0.91", {"start": v(-92, 11.55) * mm, "end": v(-92, 9.55) * mm});
            skLineSegment(sketch, "E7.1.0.92", {"start": v(-102, -4.28) * mm, "end": v(-98, -4.28) * mm});
            skLineSegment(sketch, "E7.1.0.93", {"start": v(-142, 4.27) * mm, "end": v(-138, 4.27) * mm});
            skLineSegment(sketch, "E7.1.0.94", {"start": v(-152, 11.55) * mm, "end": v(-152, 9.55) * mm});
            skLineSegment(sketch, "E7.1.0.95", {"start": v(-162, -4.28) * mm, "end": v(-158, -4.28) * mm});
            skLineSegment(sketch, "E7.1.0.96", {"start": v(-122, 9.55) * mm, "end": v(-118, 9.55) * mm});
            skLineSegment(sketch, "E7.1.0.97", {"start": v(-92, -6.28) * mm, "end": v(-88, -6.28) * mm});
            skLineSegment(sketch, "E7.1.0.98", {"start": v(-92, -9.55) * mm, "end": v(-92, -11.55) * mm});
            skLineSegment(sketch, "E7.1.0.99", {"start": v(-148, 11.55) * mm, "end": v(-148, 9.55) * mm});
            skLineSegment(sketch, "E7.1.0.100", {"start": v(-162, -9.55) * mm, "end": v(-158, -9.55) * mm});
            skLineSegment(sketch, "E7.1.0.101", {"start": v(-112, 4.27) * mm, "end": v(-108, 4.27) * mm});
            skLineSegment(sketch, "E7.1.0.102", {"start": v(-122, 11.55) * mm, "end": v(-122, 9.55) * mm});
            skLineSegment(sketch, "E7.1.0.103", {"start": v(-132, -4.28) * mm, "end": v(-128, -4.28) * mm});
            skLineSegment(sketch, "E7.1.0.104", {"start": v(-92, 9.55) * mm, "end": v(-88, 9.55) * mm});
            skLineSegment(sketch, "E7.1.0.105", {"start": v(-102, -1) * mm, "end": v(-98, -1) * mm});
            skLineSegment(sketch, "E7.1.0.106", {"start": v(-172, 4.27) * mm, "end": v(-168, 4.27) * mm});
            skLineSegment(sketch, "E7.1.0.107", {"start": v(-138, 6.27) * mm, "end": v(-138, 4.27) * mm});
            skLineSegment(sketch, "E7.1.0.108", {"start": v(-152, 9.55) * mm, "end": v(-148, 9.55) * mm});
            skLineSegment(sketch, "E7.1.0.109", {"start": v(-162, -4.28) * mm, "end": v(-162, -6.28) * mm});
            skLineSegment(sketch, "E7.1.0.110", {"start": v(-98, 1) * mm, "end": v(-98, -1) * mm});
            skLineSegment(sketch, "E7.1.0.111", {"start": v(-112, 6.27) * mm, "end": v(-108, 6.27) * mm});
            skLineSegment(sketch, "E7.1.0.112", {"start": v(-122, -6.28) * mm, "end": v(-118, -6.28) * mm});
            skLineSegment(sketch, "E7.1.0.113", {"start": v(-92, 11.55) * mm, "end": v(-88, 11.55) * mm});
            skLineSegment(sketch, "E7.1.0.114", {"start": v(-162, -11.55) * mm, "end": v(-158, -11.55) * mm});
            skLineSegment(sketch, "E7.1.0.115", {"start": v(-168, 6.27) * mm, "end": v(-168, 4.27) * mm});
            skLineSegment(sketch, "E7.1.0.116", {"start": v(-142, 6.27) * mm, "end": v(-138, 6.27) * mm});
            skLineSegment(sketch, "E7.1.0.117", {"start": v(-152, -6.28) * mm, "end": v(-148, -6.28) * mm});
            skLineSegment(sketch, "E7.1.0.118", {"start": v(-102, 1) * mm, "end": v(-98, 1) * mm});
            skLineSegment(sketch, "E7.1.0.119", {"start": v(-112, 6.27) * mm, "end": v(-112, 4.27) * mm});
            skLineSegment(sketch, "E7.1.0.120", {"start": v(-122, 11.55) * mm, "end": v(-118, 11.55) * mm});
            skLineSegment(sketch, "E7.1.0.121", {"start": v(-88, -4.28) * mm, "end": v(-88, -6.28) * mm});
            skLineSegment(sketch, "E7.1.0.122", {"start": v(-158, 1) * mm, "end": v(-158, -1) * mm});
            skLineSegment(sketch, "E7.1.0.123", {"start": v(-172, 6.27) * mm, "end": v(-168, 6.27) * mm});
            skLineSegment(sketch, "E7.1.0.124", {"start": v(-182, -6.28) * mm, "end": v(-178, -6.28) * mm});
            skLineSegment(sketch, "E7.1.0.125", {"start": v(-142, 6.27) * mm, "end": v(-142, 4.27) * mm});
            skLineSegment(sketch, "E7.1.0.126", {"start": v(-152, 11.55) * mm, "end": v(-148, 11.55) * mm});
            skLineSegment(sketch, "E7.1.0.127", {"start": v(-102, 1) * mm, "end": v(-102, -1) * mm});
            skLineSegment(sketch, "E7.1.0.128", {"start": v(-108, 11.55) * mm, "end": v(-108, 9.55) * mm});
            skLineSegment(sketch, "E7.1.0.129", {"start": v(-118, -4.28) * mm, "end": v(-118, -6.28) * mm});
            skLineSegment(sketch, "E7.1.0.130", {"start": v(-92, -4.28) * mm, "end": v(-88, -4.28) * mm});
            skLineSegment(sketch, "E7.1.0.131", {"start": v(-88, 9.55) * mm, "end": v(-88, 4.27) * mm, "construction": true});
            skLineSegment(sketch, "E7.1.0.132", {"start": v(-132, 1) * mm, "end": v(-132, -1) * mm});
            skLineSegment(sketch, "E7.1.0.133", {"start": v(-138, 11.55) * mm, "end": v(-138, 9.55) * mm});
            skLineSegment(sketch, "E7.1.0.134", {"start": v(-148, -4.28) * mm, "end": v(-148, -6.28) * mm});
            skLineSegment(sketch, "E7.1.0.135", {"start": v(-122, -4.28) * mm, "end": v(-118, -4.28) * mm});
            skLineSegment(sketch, "E7.1.0.136", {"start": v(-118, 9.55) * mm, "end": v(-118, 4.27) * mm, "construction": true});
            skLineSegment(sketch, "E7.1.0.137", {"start": v(-92, -4.28) * mm, "end": v(-92, -6.28) * mm});
            skLineSegment(sketch, "E7.1.0.138", {"start": v(-162, 1) * mm, "end": v(-158, 1) * mm});
            skLineSegment(sketch, "E7.1.0.139", {"start": v(-182, -9.55) * mm, "end": v(-182, -11.55) * mm});
            skLineSegment(sketch, "E7.1.0.140", {"start": v(-122, -4.28) * mm, "end": v(-122, -6.28) * mm});
            skLineSegment(sketch, "E7.1.0.141", {"start": v(-182, -11.55) * mm, "end": v(-172, -11.55) * mm, "construction": true});
            skLineSegment(sketch, "E7.1.0.142", {"start": v(-168, 11.55) * mm, "end": v(-168, 9.55) * mm});
            skLineSegment(sketch, "E7.1.0.143", {"start": v(-182, -9.55) * mm, "end": v(-178, -9.55) * mm});
            skLineSegment(sketch, "E7.1.0.144", {"start": v(-142, 11.55) * mm, "end": v(-142, 9.55) * mm});
            skLineSegment(sketch, "E7.1.0.145", {"start": v(-152, -4.28) * mm, "end": v(-148, -4.28) * mm});
            skLineSegment(sketch, "E7.1.0.146", {"start": v(-148, 9.55) * mm, "end": v(-148, 4.27) * mm, "construction": true});
            skLineSegment(sketch, "E7.1.0.147", {"start": v(-162, 4.27) * mm, "end": v(-158, 4.27) * mm});
            skLineSegment(sketch, "E7.1.0.148", {"start": v(-172, 11.55) * mm, "end": v(-172, 9.55) * mm});
            skLineSegment(sketch, "E7.1.0.149", {"start": v(-178, -9.55) * mm, "end": v(-178, -11.55) * mm});
            skLineSegment(sketch, "E7.1.0.150", {"start": v(-142, 9.55) * mm, "end": v(-138, 9.55) * mm});
            skLineSegment(sketch, "E7.1.0.151", {"start": v(-152, -4.28) * mm, "end": v(-152, -6.28) * mm});
            skLineSegment(sketch, "E7.1.0.152", {"start": v(-152, -1) * mm, "end": v(-148, -1) * mm});
            skLineSegment(sketch, "E7.1.0.153", {"start": v(-112, -6.28) * mm, "end": v(-108, -6.28) * mm});
            skLineSegment(sketch, "E7.1.0.154", {"start": v(-112, -9.55) * mm, "end": v(-112, -11.55) * mm});
            skLineSegment(sketch, "E7.1.0.155", {"start": v(-182, -4.28) * mm, "end": v(-182, -6.28) * mm});
            skLineSegment(sketch, "E7.1.0.156", {"start": v(-182, -4.28) * mm, "end": v(-178, -4.28) * mm});
            skLineSegment(sketch, "E7.1.0.157", {"start": v(-178, -4.28) * mm, "end": v(-178, -6.28) * mm});
            skLineSegment(sketch, "E7.1.0.158", {"start": v(-178, 6.27) * mm, "end": v(-178, 4.27) * mm});
            skLineSegment(sketch, "E7.1.0.159", {"start": v(-182, 1) * mm, "end": v(-182, -1) * mm});
            skLineSegment(sketch, "E7.1.0.160", {"start": v(-182, 1) * mm, "end": v(-178, 1) * mm});
            skLineSegment(sketch, "E7.1.0.161", {"start": v(-172, 9.55) * mm, "end": v(-168, 9.55) * mm});
            skLineSegment(sketch, "E7.1.0.162", {"start": v(-182, -11.55) * mm, "end": v(-178, -11.55) * mm});
            skLineSegment(sketch, "E7.1.0.163", {"start": v(-182, -1) * mm, "end": v(-178, -1) * mm});
            skLineSegment(sketch, "E7.1.0.164", {"start": v(-142, -6.28) * mm, "end": v(-138, -6.28) * mm});
            skLineSegment(sketch, "E7.1.0.165", {"start": v(-142, -9.55) * mm, "end": v(-142, -11.55) * mm});
            skLineSegment(sketch, "E7.1.0.166", {"start": v(-108, -9.55) * mm, "end": v(-108, -11.55) * mm});
            skLineSegment(sketch, "E7.1.0.167", {"start": v(-162, 6.27) * mm, "end": v(-158, 6.27) * mm});
            skLineSegment(sketch, "E7.1.0.168", {"start": v(-172, -6.28) * mm, "end": v(-168, -6.28) * mm});
            skLineSegment(sketch, "E7.1.0.169", {"start": v(-172, -9.55) * mm, "end": v(-172, -11.55) * mm});
            skLineSegment(sketch, "E7.1.0.170", {"start": v(-142, 11.55) * mm, "end": v(-138, 11.55) * mm});
            skLineSegment(sketch, "E7.1.0.171", {"start": v(-138, -9.55) * mm, "end": v(-138, -11.55) * mm});
            skLineSegment(sketch, "E7.1.0.172", {"start": v(-148, 1) * mm, "end": v(-148, -1) * mm});
            skLineSegment(sketch, "E7.1.0.173", {"start": v(-112, -9.55) * mm, "end": v(-108, -9.55) * mm});
            skLineSegment(sketch, "E7.1.0.174", {"start": v(-108, 9.55) * mm, "end": v(-108, 4.27) * mm, "construction": true});
            skLineSegment(sketch, "E7.1.0.175", {"start": v(-122, 1) * mm, "end": v(-122, -1) * mm});
            skLineSegment(sketch, "E7.1.0.176", {"start": v(-142, -4.28) * mm, "end": v(-142, -6.28) * mm});
            skLineSegment(sketch, "E7.1.0.177", {"start": v(-172, -1) * mm, "end": v(-168, -1) * mm});
            skLineSegment(sketch, "E7.1.0.178", {"start": v(-172, -4.28) * mm, "end": v(-172, -6.28) * mm});
            skLineSegment(sketch, "E7.1.0.179", {"start": v(-168, 1) * mm, "end": v(-168, -1) * mm});
            skLineSegment(sketch, "E7.1.0.180", {"start": v(-98, 9.55) * mm, "end": v(-98, 4.27) * mm, "construction": true});
            skLineSegment(sketch, "E7.1.0.181", {"start": v(-158, 9.55) * mm, "end": v(-158, 4.27) * mm, "construction": true});
            skLineSegment(sketch, "E7.1.0.182", {"start": v(-172, 1) * mm, "end": v(-172, -1) * mm});
            skLineSegment(sketch, "E7.1.0.183", {"start": v(-108, 6.27) * mm, "end": v(-108, 4.27) * mm});
            skLineSegment(sketch, "E7.1.0.184", {"start": v(-132, -4.28) * mm, "end": v(-132, -6.28) * mm});
            skLineSegment(sketch, "E7.1.0.185", {"start": v(-172, 1) * mm, "end": v(-168, 1) * mm});
            skLineSegment(sketch, "E7.1.0.186", {"start": v(-142, 1) * mm, "end": v(-142, -1) * mm});
            skLineSegment(sketch, "E7.1.0.187", {"start": v(-158, -4.28) * mm, "end": v(-158, -6.28) * mm});
            skLineSegment(sketch, "E7.1.0.188", {"start": v(-128, 9.55) * mm, "end": v(-128, 4.27) * mm, "construction": true});
            skLineSegment(sketch, "E7.1.0.189", {"start": v(-102, -4.28) * mm, "end": v(-102, -6.28) * mm});
            skLineSegment(sketch, "E7.1.0.190", {"start": v(-102, 4.27) * mm, "end": v(-98, 4.27) * mm});
            skLineSegment(sketch, "E7.1.0.191", {"start": v(-92, -1) * mm, "end": v(-88, -1) * mm});
            skLineSegment(sketch, "E7.1.0.192", {"start": v(-98, 6.27) * mm, "end": v(-98, 4.27) * mm});
            skLineSegment(sketch, "E7.1.0.193", {"start": v(-122, -1) * mm, "end": v(-118, -1) * mm});
            skLineSegment(sketch, "E7.1.0.194", {"start": v(-132, 4.27) * mm, "end": v(-128, 4.27) * mm});
            skLineSegment(sketch, "E7.1.0.195", {"start": v(-88, 1) * mm, "end": v(-88, -1) * mm});
            skLineSegment(sketch, "E7.1.0.196", {"start": v(-128, 6.27) * mm, "end": v(-128, 4.27) * mm});
            skLineSegment(sketch, "E7.1.0.197", {"start": v(-102, 6.27) * mm, "end": v(-98, 6.27) * mm});
            skLineSegment(sketch, "E7.1.0.198", {"start": v(-178, 11.55) * mm, "end": v(-178, 9.55) * mm});
            skLineSegment(sketch, "E7.1.0.199", {"start": v(-178, 1) * mm, "end": v(-178, -1) * mm});
            skLineSegment(sketch, "E7.1.0.200", {"start": v(-158, 6.27) * mm, "end": v(-158, 4.27) * mm});
            skLineSegment(sketch, "E7.1.0.201", {"start": v(-132, 6.27) * mm, "end": v(-128, 6.27) * mm});
            skLineSegment(sketch, "E7.1.0.202", {"start": v(-178, 9.55) * mm, "end": v(-178, 4.27) * mm, "construction": true});
            skLineSegment(sketch, "E7.1.0.203", {"start": v(-102, 6.27) * mm, "end": v(-102, 4.27) * mm});
            skLineSegment(sketch, "E7.1.0.204", {"start": v(-118, 1) * mm, "end": v(-118, -1) * mm});
            skLineSegment(sketch, "E7.1.0.205", {"start": v(-92, 1) * mm, "end": v(-88, 1) * mm});
            skLineSegment(sketch, "E7.1.0.206", {"start": v(-132, 6.27) * mm, "end": v(-132, 4.27) * mm});
            skLineSegment(sketch, "E7.1.0.207", {"start": v(-98, 11.55) * mm, "end": v(-98, 9.55) * mm});
            skLineSegment(sketch, "E7.1.0.208", {"start": v(-108, -4.28) * mm, "end": v(-108, -6.28) * mm});
            skLineSegment(sketch, "E7.1.0.209", {"start": v(-122, 1) * mm, "end": v(-118, 1) * mm});
            skLineSegment(sketch, "E7.1.0.210", {"start": v(-92, 1) * mm, "end": v(-92, -1) * mm});
            skLineSegment(sketch, "E7.2.0.0", {"start": v(-72, -9.55) * mm, "end": v(-68, -9.55) * mm});
            skLineSegment(sketch, "E7.2.0.1", {"start": v(-68, -9.55) * mm, "end": v(-68, -11.55) * mm});
            skLineSegment(sketch, "E7.2.0.2", {"start": v(-2, 11.55) * mm, "end": v(-2, 9.55) * mm});
            skLineSegment(sketch, "E7.2.0.3", {"start": v(-12, -1) * mm, "end": v(-8, -1) * mm});
            skLineSegment(sketch, "E7.2.0.4", {"start": v(-32, 11.55) * mm, "end": v(-32, 9.55) * mm});
            skLineSegment(sketch, "E7.2.0.5", {"start": v(-2, 9.55) * mm, "end": v(2, 9.55) * mm});
            skLineSegment(sketch, "E7.2.0.6", {"start": v(-62, 11.55) * mm, "end": v(-62, 9.55) * mm});
            skLineSegment(sketch, "E7.2.0.7", {"start": v(-32, 9.55) * mm, "end": v(-28, 9.55) * mm});
            skLineSegment(sketch, "E7.2.0.8", {"start": v(-2, -9.55) * mm, "end": v(-2, -11.55) * mm});
            skLineSegment(sketch, "E7.2.0.9", {"start": v(-62, 9.55) * mm, "end": v(-58, 9.55) * mm});
            skLineSegment(sketch, "E7.2.0.10", {"start": v(-8, 1) * mm, "end": v(-8, -1) * mm});
            skLineSegment(sketch, "E7.2.0.11", {"start": v(8, 6.27) * mm, "end": v(8, 4.27) * mm});
            skLineSegment(sketch, "E7.2.0.12", {"start": v(-2, 11.55) * mm, "end": v(2, 11.55) * mm});
            skLineSegment(sketch, "E7.2.0.13", {"start": v(2, -9.55) * mm, "end": v(2, -11.55) * mm});
            skLineSegment(sketch, "E7.2.0.14", {"start": v(-72, -11.55) * mm, "end": v(-68, -11.55) * mm});
            skLineSegment(sketch, "E7.2.0.15", {"start": v(-12, 1) * mm, "end": v(-8, 1) * mm});
            skLineSegment(sketch, "E7.2.0.16", {"start": v(-32, 11.55) * mm, "end": v(-28, 11.55) * mm});
            skLineSegment(sketch, "E7.2.0.17", {"start": v(-28, -9.55) * mm, "end": v(-28, -11.55) * mm});
            skLineSegment(sketch, "E7.2.0.18", {"start": v(-2, -9.55) * mm, "end": v(2, -9.55) * mm});
            skLineSegment(sketch, "E7.2.0.19", {"start": v(-62, 11.55) * mm, "end": v(-58, 11.55) * mm});
            skLineSegment(sketch, "E7.2.0.20", {"start": v(-32, -9.55) * mm, "end": v(-28, -9.55) * mm});
            skLineSegment(sketch, "E7.2.0.21", {"start": v(-32, -1) * mm, "end": v(-28, -1) * mm});
            skLineSegment(sketch, "E7.2.0.22", {"start": v(-2, -11.55) * mm, "end": v(2, -11.55) * mm});
            skLineSegment(sketch, "E7.2.0.23", {"start": v(-62, -1) * mm, "end": v(-58, -1) * mm});
            skLineSegment(sketch, "E7.2.0.24", {"start": v(-32, -11.55) * mm, "end": v(-28, -11.55) * mm});
            skLineSegment(sketch, "E7.2.0.25", {"start": v(-22, -9.55) * mm, "end": v(-22, -11.55) * mm});
            skLineSegment(sketch, "E7.2.0.26", {"start": v(12, -9.55) * mm, "end": v(12, -11.55) * mm});
            skLineSegment(sketch, "E7.2.0.27", {"start": v(-28, 1) * mm, "end": v(-28, -1) * mm});
            skLineSegment(sketch, "E7.2.0.28", {"start": v(-52, -9.55) * mm, "end": v(-52, -11.55) * mm});
            skLineSegment(sketch, "E7.2.0.29", {"start": v(-18, -9.55) * mm, "end": v(-18, -11.55) * mm});
            skLineSegment(sketch, "E7.2.0.30", {"start": v(8, -9.55) * mm, "end": v(12, -9.55) * mm});
            skLineSegment(sketch, "E7.2.0.31", {"start": v(-32, 1) * mm, "end": v(-28, 1) * mm});
            skLineSegment(sketch, "E7.2.0.32", {"start": v(-48, -9.55) * mm, "end": v(-48, -11.55) * mm});
            skLineSegment(sketch, "E7.2.0.33", {"start": v(-22, -9.55) * mm, "end": v(-18, -9.55) * mm});
            skLineSegment(sketch, "E7.2.0.34", {"start": v(-52, -9.55) * mm, "end": v(-48, -9.55) * mm});
            skLineSegment(sketch, "E7.2.0.35", {"start": v(-12, 11.55) * mm, "end": v(-12, 9.55) * mm});
            skLineSegment(sketch, "E7.2.0.36", {"start": v(-72, 6.27) * mm, "end": v(-72, 4.27) * mm});
            skLineSegment(sketch, "E7.2.0.37", {"start": v(-12, 9.55) * mm, "end": v(-8, 9.55) * mm});
            skLineSegment(sketch, "E7.2.0.38", {"start": v(8, -11.55) * mm, "end": v(12, -11.55) * mm});
            skLineSegment(sketch, "E7.2.0.39", {"start": v(-62, 1) * mm, "end": v(-62, -1) * mm});
            skLineSegment(sketch, "E7.2.0.40", {"start": v(-22, -11.55) * mm, "end": v(-18, -11.55) * mm});
            skLineSegment(sketch, "E7.2.0.41", {"start": v(-82, 11.55) * mm, "end": v(-78, 11.55) * mm});
            skLineSegment(sketch, "E7.2.0.42", {"start": v(-82, 9.55) * mm, "end": v(-78, 9.55) * mm});
            skLineSegment(sketch, "E7.2.0.43", {"start": v(-82, 11.55) * mm, "end": v(-82, 9.55) * mm});
            skLineSegment(sketch, "E7.2.0.44", {"start": v(-82, 6.27) * mm, "end": v(-82, 4.27) * mm});
            skLineSegment(sketch, "E7.2.0.45", {"start": v(-82, 6.27) * mm, "end": v(-78, 6.27) * mm});
            skLineSegment(sketch, "E7.2.0.46", {"start": v(-82, 4.27) * mm, "end": v(-78, 4.27) * mm});
            skLineSegment(sketch, "E7.2.0.47", {"start": v(-52, -11.55) * mm, "end": v(-48, -11.55) * mm});
            skLineSegment(sketch, "E7.2.0.48", {"start": v(-12, 11.55) * mm, "end": v(-8, 11.55) * mm});
            skLineSegment(sketch, "E7.2.0.49", {"start": v(-62, 6.27) * mm, "end": v(-62, 4.27) * mm});
            skLineSegment(sketch, "E7.2.0.50", {"start": v(-72, 11.55) * mm, "end": v(-68, 11.55) * mm});
            skLineSegment(sketch, "E7.2.0.51", {"start": v(-28, 11.55) * mm, "end": v(-28, 9.55) * mm});
            skLineSegment(sketch, "E7.2.0.52", {"start": v(-38, -4.28) * mm, "end": v(-38, -6.28) * mm});
            skLineSegment(sketch, "E7.2.0.53", {"start": v(-42, -9.55) * mm, "end": v(-38, -9.55) * mm});
            skLineSegment(sketch, "E7.2.0.54", {"start": v(-52, 1) * mm, "end": v(-48, 1) * mm});
            skLineSegment(sketch, "E7.2.0.55", {"start": v(-12, -4.28) * mm, "end": v(-8, -4.28) * mm});
            skLineSegment(sketch, "E7.2.0.56", {"start": v(8, 4.27) * mm, "end": v(12, 4.27) * mm});
            skLineSegment(sketch, "E7.2.0.57", {"start": v(-38, 9.55) * mm, "end": v(-38, 4.27) * mm, "construction": true});
            skLineSegment(sketch, "E7.2.0.58", {"start": v(-52, 1) * mm, "end": v(-52, -1) * mm});
            skLineSegment(sketch, "E7.2.0.59", {"start": v(-58, 11.55) * mm, "end": v(-58, 9.55) * mm});
            skLineSegment(sketch, "E7.2.0.60", {"start": v(-68, -4.28) * mm, "end": v(-68, -6.28) * mm});
            skLineSegment(sketch, "E7.2.0.61", {"start": v(-22, 4.27) * mm, "end": v(-18, 4.27) * mm});
            skLineSegment(sketch, "E7.2.0.62", {"start": v(-42, -4.28) * mm, "end": v(-38, -4.28) * mm});
            skLineSegment(sketch, "E7.2.0.63", {"start": v(12, 6.27) * mm, "end": v(12, 4.27) * mm});
            skLineSegment(sketch, "E7.2.0.64", {"start": v(-12, -4.28) * mm, "end": v(-12, -6.28) * mm});
            skLineSegment(sketch, "E7.2.0.65", {"start": v(-68, 9.55) * mm, "end": v(-68, 4.27) * mm, "construction": true});
            skLineSegment(sketch, "E7.2.0.66", {"start": v(-42, -1) * mm, "end": v(-38, -1) * mm});
            skLineSegment(sketch, "E7.2.0.67", {"start": v(-52, 4.27) * mm, "end": v(-48, 4.27) * mm});
            skLineSegment(sketch, "E7.2.0.68", {"start": v(-72, -4.28) * mm, "end": v(-68, -4.28) * mm});
            skLineSegment(sketch, "E7.2.0.69", {"start": v(-12, -11.55) * mm, "end": v(-8, -11.55) * mm});
            skLineSegment(sketch, "E7.2.0.70", {"start": v(-18, 6.27) * mm, "end": v(-18, 4.27) * mm});
            skLineSegment(sketch, "E7.2.0.71", {"start": v(8, 6.27) * mm, "end": v(12, 6.27) * mm});
            skLineSegment(sketch, "E7.2.0.72", {"start": v(-2, -6.28) * mm, "end": v(2, -6.28) * mm});
            skLineSegment(sketch, "E7.2.0.73", {"start": v(-42, -11.55) * mm, "end": v(-38, -11.55) * mm});
            skLineSegment(sketch, "E7.2.0.74", {"start": v(-48, 6.27) * mm, "end": v(-48, 4.27) * mm});
            skLineSegment(sketch, "E7.2.0.75", {"start": v(-22, 6.27) * mm, "end": v(-18, 6.27) * mm});
            skLineSegment(sketch, "E7.2.0.76", {"start": v(-32, -6.28) * mm, "end": v(-28, -6.28) * mm});
            skLineSegment(sketch, "E7.2.0.77", {"start": v(-32, -9.55) * mm, "end": v(-32, -11.55) * mm});
            skLineSegment(sketch, "E7.2.0.78", {"start": v(-38, 1) * mm, "end": v(-38, -1) * mm});
            skLineSegment(sketch, "E7.2.0.79", {"start": v(-52, 6.27) * mm, "end": v(-48, 6.27) * mm});
            skLineSegment(sketch, "E7.2.0.80", {"start": v(-62, -6.28) * mm, "end": v(-58, -6.28) * mm});
            skLineSegment(sketch, "E7.2.0.81", {"start": v(-62, -9.55) * mm, "end": v(-62, -11.55) * mm});
            skLineSegment(sketch, "E7.2.0.82", {"start": v(-22, 6.27) * mm, "end": v(-22, 4.27) * mm});
            skLineSegment(sketch, "E7.2.0.83", {"start": v(12, 11.55) * mm, "end": v(12, 9.55) * mm});
            skLineSegment(sketch, "E7.2.0.84", {"start": v(2, -4.28) * mm, "end": v(2, -6.28) * mm});
            skLineSegment(sketch, "E7.2.0.85", {"start": v(-42, 1) * mm, "end": v(-38, 1) * mm});
            skLineSegment(sketch, "E7.2.0.86", {"start": v(-52, 6.27) * mm, "end": v(-52, 4.27) * mm});
            skLineSegment(sketch, "E7.2.0.87", {"start": v(-58, -9.55) * mm, "end": v(-58, -11.55) * mm});
            skLineSegment(sketch, "E7.2.0.88", {"start": v(-12, 1) * mm, "end": v(-12, -1) * mm});
            skLineSegment(sketch, "E7.2.0.89", {"start": v(-18, 11.55) * mm, "end": v(-18, 9.55) * mm});
            skLineSegment(sketch, "E7.2.0.90", {"start": v(-28, -4.28) * mm, "end": v(-28, -6.28) * mm});
            skLineSegment(sketch, "E7.2.0.91", {"start": v(8, 11.55) * mm, "end": v(8, 9.55) * mm});
            skLineSegment(sketch, "E7.2.0.92", {"start": v(-2, -4.28) * mm, "end": v(2, -4.28) * mm});
            skLineSegment(sketch, "E7.2.0.93", {"start": v(-42, 4.27) * mm, "end": v(-38, 4.27) * mm});
            skLineSegment(sketch, "E7.2.0.94", {"start": v(-52, 11.55) * mm, "end": v(-52, 9.55) * mm});
            skLineSegment(sketch, "E7.2.0.95", {"start": v(-62, -4.28) * mm, "end": v(-58, -4.28) * mm});
            skLineSegment(sketch, "E7.2.0.96", {"start": v(-22, 9.55) * mm, "end": v(-18, 9.55) * mm});
            skLineSegment(sketch, "E7.2.0.97", {"start": v(8, -6.28) * mm, "end": v(12, -6.28) * mm});
            skLineSegment(sketch, "E7.2.0.98", {"start": v(8, -9.55) * mm, "end": v(8, -11.55) * mm});
            skLineSegment(sketch, "E7.2.0.99", {"start": v(-48, 11.55) * mm, "end": v(-48, 9.55) * mm});
            skLineSegment(sketch, "E7.2.0.100", {"start": v(-62, -9.55) * mm, "end": v(-58, -9.55) * mm});
            skLineSegment(sketch, "E7.2.0.101", {"start": v(-12, 4.27) * mm, "end": v(-8, 4.27) * mm});
            skLineSegment(sketch, "E7.2.0.102", {"start": v(-22, 11.55) * mm, "end": v(-22, 9.55) * mm});
            skLineSegment(sketch, "E7.2.0.103", {"start": v(-32, -4.28) * mm, "end": v(-28, -4.28) * mm});
            skLineSegment(sketch, "E7.2.0.104", {"start": v(8, 9.55) * mm, "end": v(12, 9.55) * mm});
            skLineSegment(sketch, "E7.2.0.105", {"start": v(-2, -1) * mm, "end": v(2, -1) * mm});
            skLineSegment(sketch, "E7.2.0.106", {"start": v(-72, 4.27) * mm, "end": v(-68, 4.27) * mm});
            skLineSegment(sketch, "E7.2.0.107", {"start": v(-38, 6.27) * mm, "end": v(-38, 4.27) * mm});
            skLineSegment(sketch, "E7.2.0.108", {"start": v(-52, 9.55) * mm, "end": v(-48, 9.55) * mm});
            skLineSegment(sketch, "E7.2.0.109", {"start": v(-62, -4.28) * mm, "end": v(-62, -6.28) * mm});
            skLineSegment(sketch, "E7.2.0.110", {"start": v(2, 1) * mm, "end": v(2, -1) * mm});
            skLineSegment(sketch, "E7.2.0.111", {"start": v(-12, 6.27) * mm, "end": v(-8, 6.27) * mm});
            skLineSegment(sketch, "E7.2.0.112", {"start": v(-22, -6.28) * mm, "end": v(-18, -6.28) * mm});
            skLineSegment(sketch, "E7.2.0.113", {"start": v(8, 11.55) * mm, "end": v(12, 11.55) * mm});
            skLineSegment(sketch, "E7.2.0.114", {"start": v(-62, -11.55) * mm, "end": v(-58, -11.55) * mm});
            skLineSegment(sketch, "E7.2.0.115", {"start": v(-68, 6.27) * mm, "end": v(-68, 4.27) * mm});
            skLineSegment(sketch, "E7.2.0.116", {"start": v(-42, 6.27) * mm, "end": v(-38, 6.27) * mm});
            skLineSegment(sketch, "E7.2.0.117", {"start": v(-52, -6.28) * mm, "end": v(-48, -6.28) * mm});
            skLineSegment(sketch, "E7.2.0.118", {"start": v(-2, 1) * mm, "end": v(2, 1) * mm});
            skLineSegment(sketch, "E7.2.0.119", {"start": v(-12, 6.27) * mm, "end": v(-12, 4.27) * mm});
            skLineSegment(sketch, "E7.2.0.120", {"start": v(-22, 11.55) * mm, "end": v(-18, 11.55) * mm});
            skLineSegment(sketch, "E7.2.0.121", {"start": v(12, -4.28) * mm, "end": v(12, -6.28) * mm});
            skLineSegment(sketch, "E7.2.0.122", {"start": v(-58, 1) * mm, "end": v(-58, -1) * mm});
            skLineSegment(sketch, "E7.2.0.123", {"start": v(-72, 6.27) * mm, "end": v(-68, 6.27) * mm});
            skLineSegment(sketch, "E7.2.0.124", {"start": v(-82, -6.28) * mm, "end": v(-78, -6.28) * mm});
            skLineSegment(sketch, "E7.2.0.125", {"start": v(-42, 6.27) * mm, "end": v(-42, 4.27) * mm});
            skLineSegment(sketch, "E7.2.0.126", {"start": v(-52, 11.55) * mm, "end": v(-48, 11.55) * mm});
            skLineSegment(sketch, "E7.2.0.127", {"start": v(-2, 1) * mm, "end": v(-2, -1) * mm});
            skLineSegment(sketch, "E7.2.0.128", {"start": v(-8, 11.55) * mm, "end": v(-8, 9.55) * mm});
            skLineSegment(sketch, "E7.2.0.129", {"start": v(-18, -4.28) * mm, "end": v(-18, -6.28) * mm});
            skLineSegment(sketch, "E7.2.0.130", {"start": v(8, -4.28) * mm, "end": v(12, -4.28) * mm});
            skLineSegment(sketch, "E7.2.0.131", {"start": v(12, 9.55) * mm, "end": v(12, 4.27) * mm, "construction": true});
            skLineSegment(sketch, "E7.2.0.132", {"start": v(-32, 1) * mm, "end": v(-32, -1) * mm});
            skLineSegment(sketch, "E7.2.0.133", {"start": v(-38, 11.55) * mm, "end": v(-38, 9.55) * mm});
            skLineSegment(sketch, "E7.2.0.134", {"start": v(-48, -4.28) * mm, "end": v(-48, -6.28) * mm});
            skLineSegment(sketch, "E7.2.0.135", {"start": v(-22, -4.28) * mm, "end": v(-18, -4.28) * mm});
            skLineSegment(sketch, "E7.2.0.136", {"start": v(-18, 9.55) * mm, "end": v(-18, 4.27) * mm, "construction": true});
            skLineSegment(sketch, "E7.2.0.137", {"start": v(8, -4.28) * mm, "end": v(8, -6.28) * mm});
            skLineSegment(sketch, "E7.2.0.138", {"start": v(-62, 1) * mm, "end": v(-58, 1) * mm});
            skLineSegment(sketch, "E7.2.0.139", {"start": v(-82, -9.55) * mm, "end": v(-82, -11.55) * mm});
            skLineSegment(sketch, "E7.2.0.140", {"start": v(-22, -4.28) * mm, "end": v(-22, -6.28) * mm});
            skLineSegment(sketch, "E7.2.0.141", {"start": v(-82, -11.55) * mm, "end": v(-72, -11.55) * mm, "construction": true});
            skLineSegment(sketch, "E7.2.0.142", {"start": v(-68, 11.55) * mm, "end": v(-68, 9.55) * mm});
            skLineSegment(sketch, "E7.2.0.143", {"start": v(-82, -9.55) * mm, "end": v(-78, -9.55) * mm});
            skLineSegment(sketch, "E7.2.0.144", {"start": v(-42, 11.55) * mm, "end": v(-42, 9.55) * mm});
            skLineSegment(sketch, "E7.2.0.145", {"start": v(-52, -4.28) * mm, "end": v(-48, -4.28) * mm});
            skLineSegment(sketch, "E7.2.0.146", {"start": v(-48, 9.55) * mm, "end": v(-48, 4.27) * mm, "construction": true});
            skLineSegment(sketch, "E7.2.0.147", {"start": v(-62, 4.27) * mm, "end": v(-58, 4.27) * mm});
            skLineSegment(sketch, "E7.2.0.148", {"start": v(-72, 11.55) * mm, "end": v(-72, 9.55) * mm});
            skLineSegment(sketch, "E7.2.0.149", {"start": v(-78, -9.55) * mm, "end": v(-78, -11.55) * mm});
            skLineSegment(sketch, "E7.2.0.150", {"start": v(-42, 9.55) * mm, "end": v(-38, 9.55) * mm});
            skLineSegment(sketch, "E7.2.0.151", {"start": v(-52, -4.28) * mm, "end": v(-52, -6.28) * mm});
            skLineSegment(sketch, "E7.2.0.152", {"start": v(-52, -1) * mm, "end": v(-48, -1) * mm});
            skLineSegment(sketch, "E7.2.0.153", {"start": v(-12, -6.28) * mm, "end": v(-8, -6.28) * mm});
            skLineSegment(sketch, "E7.2.0.154", {"start": v(-12, -9.55) * mm, "end": v(-12, -11.55) * mm});
            skLineSegment(sketch, "E7.2.0.155", {"start": v(-82, -4.28) * mm, "end": v(-82, -6.28) * mm});
            skLineSegment(sketch, "E7.2.0.156", {"start": v(-82, -4.28) * mm, "end": v(-78, -4.28) * mm});
            skLineSegment(sketch, "E7.2.0.157", {"start": v(-78, -4.28) * mm, "end": v(-78, -6.28) * mm});
            skLineSegment(sketch, "E7.2.0.158", {"start": v(-78, 6.27) * mm, "end": v(-78, 4.27) * mm});
            skLineSegment(sketch, "E7.2.0.159", {"start": v(-82, 1) * mm, "end": v(-82, -1) * mm});
            skLineSegment(sketch, "E7.2.0.160", {"start": v(-82, 1) * mm, "end": v(-78, 1) * mm});
            skLineSegment(sketch, "E7.2.0.161", {"start": v(-72, 9.55) * mm, "end": v(-68, 9.55) * mm});
            skLineSegment(sketch, "E7.2.0.162", {"start": v(-82, -11.55) * mm, "end": v(-78, -11.55) * mm});
            skLineSegment(sketch, "E7.2.0.163", {"start": v(-82, -1) * mm, "end": v(-78, -1) * mm});
            skLineSegment(sketch, "E7.2.0.164", {"start": v(-42, -6.28) * mm, "end": v(-38, -6.28) * mm});
            skLineSegment(sketch, "E7.2.0.165", {"start": v(-42, -9.55) * mm, "end": v(-42, -11.55) * mm});
            skLineSegment(sketch, "E7.2.0.166", {"start": v(-8, -9.55) * mm, "end": v(-8, -11.55) * mm});
            skLineSegment(sketch, "E7.2.0.167", {"start": v(-62, 6.27) * mm, "end": v(-58, 6.27) * mm});
            skLineSegment(sketch, "E7.2.0.168", {"start": v(-72, -6.28) * mm, "end": v(-68, -6.28) * mm});
            skLineSegment(sketch, "E7.2.0.169", {"start": v(-72, -9.55) * mm, "end": v(-72, -11.55) * mm});
            skLineSegment(sketch, "E7.2.0.170", {"start": v(-42, 11.55) * mm, "end": v(-38, 11.55) * mm});
            skLineSegment(sketch, "E7.2.0.171", {"start": v(-38, -9.55) * mm, "end": v(-38, -11.55) * mm});
            skLineSegment(sketch, "E7.2.0.172", {"start": v(-48, 1) * mm, "end": v(-48, -1) * mm});
            skLineSegment(sketch, "E7.2.0.173", {"start": v(-12, -9.55) * mm, "end": v(-8, -9.55) * mm});
            skLineSegment(sketch, "E7.2.0.174", {"start": v(-8, 9.55) * mm, "end": v(-8, 4.27) * mm, "construction": true});
            skLineSegment(sketch, "E7.2.0.175", {"start": v(-22, 1) * mm, "end": v(-22, -1) * mm});
            skLineSegment(sketch, "E7.2.0.176", {"start": v(-42, -4.28) * mm, "end": v(-42, -6.28) * mm});
            skLineSegment(sketch, "E7.2.0.177", {"start": v(-72, -1) * mm, "end": v(-68, -1) * mm});
            skLineSegment(sketch, "E7.2.0.178", {"start": v(-72, -4.28) * mm, "end": v(-72, -6.28) * mm});
            skLineSegment(sketch, "E7.2.0.179", {"start": v(-68, 1) * mm, "end": v(-68, -1) * mm});
            skLineSegment(sketch, "E7.2.0.180", {"start": v(2, 9.55) * mm, "end": v(2, 4.27) * mm, "construction": true});
            skLineSegment(sketch, "E7.2.0.181", {"start": v(-58, 9.55) * mm, "end": v(-58, 4.27) * mm, "construction": true});
            skLineSegment(sketch, "E7.2.0.182", {"start": v(-72, 1) * mm, "end": v(-72, -1) * mm});
            skLineSegment(sketch, "E7.2.0.183", {"start": v(-8, 6.27) * mm, "end": v(-8, 4.27) * mm});
            skLineSegment(sketch, "E7.2.0.184", {"start": v(-32, -4.28) * mm, "end": v(-32, -6.28) * mm});
            skLineSegment(sketch, "E7.2.0.185", {"start": v(-72, 1) * mm, "end": v(-68, 1) * mm});
            skLineSegment(sketch, "E7.2.0.186", {"start": v(-42, 1) * mm, "end": v(-42, -1) * mm});
            skLineSegment(sketch, "E7.2.0.187", {"start": v(-58, -4.28) * mm, "end": v(-58, -6.28) * mm});
            skLineSegment(sketch, "E7.2.0.188", {"start": v(-28, 9.55) * mm, "end": v(-28, 4.27) * mm, "construction": true});
            skLineSegment(sketch, "E7.2.0.189", {"start": v(-2, -4.28) * mm, "end": v(-2, -6.28) * mm});
            skLineSegment(sketch, "E7.2.0.190", {"start": v(-2, 4.27) * mm, "end": v(2, 4.27) * mm});
            skLineSegment(sketch, "E7.2.0.191", {"start": v(8, -1) * mm, "end": v(12, -1) * mm});
            skLineSegment(sketch, "E7.2.0.192", {"start": v(2, 6.27) * mm, "end": v(2, 4.27) * mm});
            skLineSegment(sketch, "E7.2.0.193", {"start": v(-22, -1) * mm, "end": v(-18, -1) * mm});
            skLineSegment(sketch, "E7.2.0.194", {"start": v(-32, 4.27) * mm, "end": v(-28, 4.27) * mm});
            skLineSegment(sketch, "E7.2.0.195", {"start": v(12, 1) * mm, "end": v(12, -1) * mm});
            skLineSegment(sketch, "E7.2.0.196", {"start": v(-28, 6.27) * mm, "end": v(-28, 4.27) * mm});
            skLineSegment(sketch, "E7.2.0.197", {"start": v(-2, 6.27) * mm, "end": v(2, 6.27) * mm});
            skLineSegment(sketch, "E7.2.0.198", {"start": v(-78, 11.55) * mm, "end": v(-78, 9.55) * mm});
            skLineSegment(sketch, "E7.2.0.199", {"start": v(-78, 1) * mm, "end": v(-78, -1) * mm});
            skLineSegment(sketch, "E7.2.0.200", {"start": v(-58, 6.27) * mm, "end": v(-58, 4.27) * mm});
            skLineSegment(sketch, "E7.2.0.201", {"start": v(-32, 6.27) * mm, "end": v(-28, 6.27) * mm});
            skLineSegment(sketch, "E7.2.0.202", {"start": v(-78, 9.55) * mm, "end": v(-78, 4.27) * mm, "construction": true});
            skLineSegment(sketch, "E7.2.0.203", {"start": v(-2, 6.27) * mm, "end": v(-2, 4.27) * mm});
            skLineSegment(sketch, "E7.2.0.204", {"start": v(-18, 1) * mm, "end": v(-18, -1) * mm});
            skLineSegment(sketch, "E7.2.0.205", {"start": v(8, 1) * mm, "end": v(12, 1) * mm});
            skLineSegment(sketch, "E7.2.0.206", {"start": v(-32, 6.27) * mm, "end": v(-32, 4.27) * mm});
            skLineSegment(sketch, "E7.2.0.207", {"start": v(2, 11.55) * mm, "end": v(2, 9.55) * mm});
            skLineSegment(sketch, "E7.2.0.208", {"start": v(-8, -4.28) * mm, "end": v(-8, -6.28) * mm});
            skLineSegment(sketch, "E7.2.0.209", {"start": v(-22, 1) * mm, "end": v(-18, 1) * mm});
            skLineSegment(sketch, "E7.2.0.210", {"start": v(8, 1) * mm, "end": v(8, -1) * mm});
            skLineSegment(sketch, "E7.3.0.0", {"start": v(28, -9.55) * mm, "end": v(32, -9.55) * mm});
            skLineSegment(sketch, "E7.3.0.1", {"start": v(32, -9.55) * mm, "end": v(32, -11.55) * mm});
            skLineSegment(sketch, "E7.3.0.2", {"start": v(98, 11.55) * mm, "end": v(98, 9.55) * mm});
            skLineSegment(sketch, "E7.3.0.3", {"start": v(88, -1) * mm, "end": v(92, -1) * mm});
            skLineSegment(sketch, "E7.3.0.4", {"start": v(68, 11.55) * mm, "end": v(68, 9.55) * mm});
            skLineSegment(sketch, "E7.3.0.5", {"start": v(98, 9.55) * mm, "end": v(102, 9.55) * mm});
            skLineSegment(sketch, "E7.3.0.6", {"start": v(38, 11.55) * mm, "end": v(38, 9.55) * mm});
            skLineSegment(sketch, "E7.3.0.7", {"start": v(68, 9.55) * mm, "end": v(72, 9.55) * mm});
            skLineSegment(sketch, "E7.3.0.8", {"start": v(98, -9.55) * mm, "end": v(98, -11.55) * mm});
            skLineSegment(sketch, "E7.3.0.9", {"start": v(38, 9.55) * mm, "end": v(42, 9.55) * mm});
            skLineSegment(sketch, "E7.3.0.10", {"start": v(92, 1) * mm, "end": v(92, -1) * mm});
            skLineSegment(sketch, "E7.3.0.11", {"start": v(108, 6.27) * mm, "end": v(108, 4.27) * mm});
            skLineSegment(sketch, "E7.3.0.12", {"start": v(98, 11.55) * mm, "end": v(102, 11.55) * mm});
            skLineSegment(sketch, "E7.3.0.13", {"start": v(102, -9.55) * mm, "end": v(102, -11.55) * mm});
            skLineSegment(sketch, "E7.3.0.14", {"start": v(28, -11.55) * mm, "end": v(32, -11.55) * mm});
            skLineSegment(sketch, "E7.3.0.15", {"start": v(88, 1) * mm, "end": v(92, 1) * mm});
            skLineSegment(sketch, "E7.3.0.16", {"start": v(68, 11.55) * mm, "end": v(72, 11.55) * mm});
            skLineSegment(sketch, "E7.3.0.17", {"start": v(72, -9.55) * mm, "end": v(72, -11.55) * mm});
            skLineSegment(sketch, "E7.3.0.18", {"start": v(98, -9.55) * mm, "end": v(102, -9.55) * mm});
            skLineSegment(sketch, "E7.3.0.19", {"start": v(38, 11.55) * mm, "end": v(42, 11.55) * mm});
            skLineSegment(sketch, "E7.3.0.20", {"start": v(68, -9.55) * mm, "end": v(72, -9.55) * mm});
            skLineSegment(sketch, "E7.3.0.21", {"start": v(68, -1) * mm, "end": v(72, -1) * mm});
            skLineSegment(sketch, "E7.3.0.22", {"start": v(98, -11.55) * mm, "end": v(102, -11.55) * mm});
            skLineSegment(sketch, "E7.3.0.23", {"start": v(38, -1) * mm, "end": v(42, -1) * mm});
            skLineSegment(sketch, "E7.3.0.24", {"start": v(68, -11.55) * mm, "end": v(72, -11.55) * mm});
            skLineSegment(sketch, "E7.3.0.25", {"start": v(78, -9.55) * mm, "end": v(78, -11.55) * mm});
            skLineSegment(sketch, "E7.3.0.26", {"start": v(112, -9.55) * mm, "end": v(112, -11.55) * mm});
            skLineSegment(sketch, "E7.3.0.27", {"start": v(72, 1) * mm, "end": v(72, -1) * mm});
            skLineSegment(sketch, "E7.3.0.28", {"start": v(48, -9.55) * mm, "end": v(48, -11.55) * mm});
            skLineSegment(sketch, "E7.3.0.29", {"start": v(82, -9.55) * mm, "end": v(82, -11.55) * mm});
            skLineSegment(sketch, "E7.3.0.30", {"start": v(108, -9.55) * mm, "end": v(112, -9.55) * mm});
            skLineSegment(sketch, "E7.3.0.31", {"start": v(68, 1) * mm, "end": v(72, 1) * mm});
            skLineSegment(sketch, "E7.3.0.32", {"start": v(52, -9.55) * mm, "end": v(52, -11.55) * mm});
            skLineSegment(sketch, "E7.3.0.33", {"start": v(78, -9.55) * mm, "end": v(82, -9.55) * mm});
            skLineSegment(sketch, "E7.3.0.34", {"start": v(48, -9.55) * mm, "end": v(52, -9.55) * mm});
            skLineSegment(sketch, "E7.3.0.35", {"start": v(88, 11.55) * mm, "end": v(88, 9.55) * mm});
            skLineSegment(sketch, "E7.3.0.36", {"start": v(28, 6.27) * mm, "end": v(28, 4.27) * mm});
            skLineSegment(sketch, "E7.3.0.37", {"start": v(88, 9.55) * mm, "end": v(92, 9.55) * mm});
            skLineSegment(sketch, "E7.3.0.38", {"start": v(108, -11.55) * mm, "end": v(112, -11.55) * mm});
            skLineSegment(sketch, "E7.3.0.39", {"start": v(38, 1) * mm, "end": v(38, -1) * mm});
            skLineSegment(sketch, "E7.3.0.40", {"start": v(78, -11.55) * mm, "end": v(82, -11.55) * mm});
            skLineSegment(sketch, "E7.3.0.41", {"start": v(18, 11.55) * mm, "end": v(22, 11.55) * mm});
            skLineSegment(sketch, "E7.3.0.42", {"start": v(18, 9.55) * mm, "end": v(22, 9.55) * mm});
            skLineSegment(sketch, "E7.3.0.43", {"start": v(18, 11.55) * mm, "end": v(18, 9.55) * mm});
            skLineSegment(sketch, "E7.3.0.44", {"start": v(18, 6.27) * mm, "end": v(18, 4.27) * mm});
            skLineSegment(sketch, "E7.3.0.45", {"start": v(18, 6.27) * mm, "end": v(22, 6.27) * mm});
            skLineSegment(sketch, "E7.3.0.46", {"start": v(18, 4.27) * mm, "end": v(22, 4.27) * mm});
            skLineSegment(sketch, "E7.3.0.47", {"start": v(48, -11.55) * mm, "end": v(52, -11.55) * mm});
            skLineSegment(sketch, "E7.3.0.48", {"start": v(88, 11.55) * mm, "end": v(92, 11.55) * mm});
            skLineSegment(sketch, "E7.3.0.49", {"start": v(38, 6.27) * mm, "end": v(38, 4.27) * mm});
            skLineSegment(sketch, "E7.3.0.50", {"start": v(28, 11.55) * mm, "end": v(32, 11.55) * mm});
            skLineSegment(sketch, "E7.3.0.51", {"start": v(72, 11.55) * mm, "end": v(72, 9.55) * mm});
            skLineSegment(sketch, "E7.3.0.52", {"start": v(62, -4.28) * mm, "end": v(62, -6.28) * mm});
            skLineSegment(sketch, "E7.3.0.53", {"start": v(58, -9.55) * mm, "end": v(62, -9.55) * mm});
            skLineSegment(sketch, "E7.3.0.54", {"start": v(48, 1) * mm, "end": v(52, 1) * mm});
            skLineSegment(sketch, "E7.3.0.55", {"start": v(88, -4.28) * mm, "end": v(92, -4.28) * mm});
            skLineSegment(sketch, "E7.3.0.56", {"start": v(108, 4.27) * mm, "end": v(112, 4.27) * mm});
            skLineSegment(sketch, "E7.3.0.57", {"start": v(62, 9.55) * mm, "end": v(62, 4.27) * mm, "construction": true});
            skLineSegment(sketch, "E7.3.0.58", {"start": v(48, 1) * mm, "end": v(48, -1) * mm});
            skLineSegment(sketch, "E7.3.0.59", {"start": v(42, 11.55) * mm, "end": v(42, 9.55) * mm});
            skLineSegment(sketch, "E7.3.0.60", {"start": v(32, -4.28) * mm, "end": v(32, -6.28) * mm});
            skLineSegment(sketch, "E7.3.0.61", {"start": v(78, 4.27) * mm, "end": v(82, 4.27) * mm});
            skLineSegment(sketch, "E7.3.0.62", {"start": v(58, -4.28) * mm, "end": v(62, -4.28) * mm});
            skLineSegment(sketch, "E7.3.0.63", {"start": v(112, 6.27) * mm, "end": v(112, 4.27) * mm});
            skLineSegment(sketch, "E7.3.0.64", {"start": v(88, -4.28) * mm, "end": v(88, -6.28) * mm});
            skLineSegment(sketch, "E7.3.0.65", {"start": v(32, 9.55) * mm, "end": v(32, 4.27) * mm, "construction": true});
            skLineSegment(sketch, "E7.3.0.66", {"start": v(58, -1) * mm, "end": v(62, -1) * mm});
            skLineSegment(sketch, "E7.3.0.67", {"start": v(48, 4.27) * mm, "end": v(52, 4.27) * mm});
            skLineSegment(sketch, "E7.3.0.68", {"start": v(28, -4.28) * mm, "end": v(32, -4.28) * mm});
            skLineSegment(sketch, "E7.3.0.69", {"start": v(88, -11.55) * mm, "end": v(92, -11.55) * mm});
            skLineSegment(sketch, "E7.3.0.70", {"start": v(82, 6.27) * mm, "end": v(82, 4.27) * mm});
            skLineSegment(sketch, "E7.3.0.71", {"start": v(108, 6.27) * mm, "end": v(112, 6.27) * mm});
            skLineSegment(sketch, "E7.3.0.72", {"start": v(98, -6.28) * mm, "end": v(102, -6.28) * mm});
            skLineSegment(sketch, "E7.3.0.73", {"start": v(58, -11.55) * mm, "end": v(62, -11.55) * mm});
            skLineSegment(sketch, "E7.3.0.74", {"start": v(52, 6.27) * mm, "end": v(52, 4.27) * mm});
            skLineSegment(sketch, "E7.3.0.75", {"start": v(78, 6.27) * mm, "end": v(82, 6.27) * mm});
            skLineSegment(sketch, "E7.3.0.76", {"start": v(68, -6.28) * mm, "end": v(72, -6.28) * mm});
            skLineSegment(sketch, "E7.3.0.77", {"start": v(68, -9.55) * mm, "end": v(68, -11.55) * mm});
            skLineSegment(sketch, "E7.3.0.78", {"start": v(62, 1) * mm, "end": v(62, -1) * mm});
            skLineSegment(sketch, "E7.3.0.79", {"start": v(48, 6.27) * mm, "end": v(52, 6.27) * mm});
            skLineSegment(sketch, "E7.3.0.80", {"start": v(38, -6.28) * mm, "end": v(42, -6.28) * mm});
            skLineSegment(sketch, "E7.3.0.81", {"start": v(38, -9.55) * mm, "end": v(38, -11.55) * mm});
            skLineSegment(sketch, "E7.3.0.82", {"start": v(78, 6.27) * mm, "end": v(78, 4.27) * mm});
            skLineSegment(sketch, "E7.3.0.83", {"start": v(112, 11.55) * mm, "end": v(112, 9.55) * mm});
            skLineSegment(sketch, "E7.3.0.84", {"start": v(102, -4.28) * mm, "end": v(102, -6.28) * mm});
            skLineSegment(sketch, "E7.3.0.85", {"start": v(58, 1) * mm, "end": v(62, 1) * mm});
            skLineSegment(sketch, "E7.3.0.86", {"start": v(48, 6.27) * mm, "end": v(48, 4.27) * mm});
            skLineSegment(sketch, "E7.3.0.87", {"start": v(42, -9.55) * mm, "end": v(42, -11.55) * mm});
            skLineSegment(sketch, "E7.3.0.88", {"start": v(88, 1) * mm, "end": v(88, -1) * mm});
            skLineSegment(sketch, "E7.3.0.89", {"start": v(82, 11.55) * mm, "end": v(82, 9.55) * mm});
            skLineSegment(sketch, "E7.3.0.90", {"start": v(72, -4.28) * mm, "end": v(72, -6.28) * mm});
            skLineSegment(sketch, "E7.3.0.91", {"start": v(108, 11.55) * mm, "end": v(108, 9.55) * mm});
            skLineSegment(sketch, "E7.3.0.92", {"start": v(98, -4.28) * mm, "end": v(102, -4.28) * mm});
            skLineSegment(sketch, "E7.3.0.93", {"start": v(58, 4.27) * mm, "end": v(62, 4.27) * mm});
            skLineSegment(sketch, "E7.3.0.94", {"start": v(48, 11.55) * mm, "end": v(48, 9.55) * mm});
            skLineSegment(sketch, "E7.3.0.95", {"start": v(38, -4.28) * mm, "end": v(42, -4.28) * mm});
            skLineSegment(sketch, "E7.3.0.96", {"start": v(78, 9.55) * mm, "end": v(82, 9.55) * mm});
            skLineSegment(sketch, "E7.3.0.97", {"start": v(108, -6.28) * mm, "end": v(112, -6.28) * mm});
            skLineSegment(sketch, "E7.3.0.98", {"start": v(108, -9.55) * mm, "end": v(108, -11.55) * mm});
            skLineSegment(sketch, "E7.3.0.99", {"start": v(52, 11.55) * mm, "end": v(52, 9.55) * mm});
            skLineSegment(sketch, "E7.3.0.100", {"start": v(38, -9.55) * mm, "end": v(42, -9.55) * mm});
            skLineSegment(sketch, "E7.3.0.101", {"start": v(88, 4.27) * mm, "end": v(92, 4.27) * mm});
            skLineSegment(sketch, "E7.3.0.102", {"start": v(78, 11.55) * mm, "end": v(78, 9.55) * mm});
            skLineSegment(sketch, "E7.3.0.103", {"start": v(68, -4.28) * mm, "end": v(72, -4.28) * mm});
            skLineSegment(sketch, "E7.3.0.104", {"start": v(108, 9.55) * mm, "end": v(112, 9.55) * mm});
            skLineSegment(sketch, "E7.3.0.105", {"start": v(98, -1) * mm, "end": v(102, -1) * mm});
            skLineSegment(sketch, "E7.3.0.106", {"start": v(28, 4.27) * mm, "end": v(32, 4.27) * mm});
            skLineSegment(sketch, "E7.3.0.107", {"start": v(62, 6.27) * mm, "end": v(62, 4.27) * mm});
            skLineSegment(sketch, "E7.3.0.108", {"start": v(48, 9.55) * mm, "end": v(52, 9.55) * mm});
            skLineSegment(sketch, "E7.3.0.109", {"start": v(38, -4.28) * mm, "end": v(38, -6.28) * mm});
            skLineSegment(sketch, "E7.3.0.110", {"start": v(102, 1) * mm, "end": v(102, -1) * mm});
            skLineSegment(sketch, "E7.3.0.111", {"start": v(88, 6.27) * mm, "end": v(92, 6.27) * mm});
            skLineSegment(sketch, "E7.3.0.112", {"start": v(78, -6.28) * mm, "end": v(82, -6.28) * mm});
            skLineSegment(sketch, "E7.3.0.113", {"start": v(108, 11.55) * mm, "end": v(112, 11.55) * mm});
            skLineSegment(sketch, "E7.3.0.114", {"start": v(38, -11.55) * mm, "end": v(42, -11.55) * mm});
            skLineSegment(sketch, "E7.3.0.115", {"start": v(32, 6.27) * mm, "end": v(32, 4.27) * mm});
            skLineSegment(sketch, "E7.3.0.116", {"start": v(58, 6.27) * mm, "end": v(62, 6.27) * mm});
            skLineSegment(sketch, "E7.3.0.117", {"start": v(48, -6.28) * mm, "end": v(52, -6.28) * mm});
            skLineSegment(sketch, "E7.3.0.118", {"start": v(98, 1) * mm, "end": v(102, 1) * mm});
            skLineSegment(sketch, "E7.3.0.119", {"start": v(88, 6.27) * mm, "end": v(88, 4.27) * mm});
            skLineSegment(sketch, "E7.3.0.120", {"start": v(78, 11.55) * mm, "end": v(82, 11.55) * mm});
            skLineSegment(sketch, "E7.3.0.121", {"start": v(112, -4.28) * mm, "end": v(112, -6.28) * mm});
            skLineSegment(sketch, "E7.3.0.122", {"start": v(42, 1) * mm, "end": v(42, -1) * mm});
            skLineSegment(sketch, "E7.3.0.123", {"start": v(28, 6.27) * mm, "end": v(32, 6.27) * mm});
            skLineSegment(sketch, "E7.3.0.124", {"start": v(18, -6.28) * mm, "end": v(22, -6.28) * mm});
            skLineSegment(sketch, "E7.3.0.125", {"start": v(58, 6.27) * mm, "end": v(58, 4.27) * mm});
            skLineSegment(sketch, "E7.3.0.126", {"start": v(48, 11.55) * mm, "end": v(52, 11.55) * mm});
            skLineSegment(sketch, "E7.3.0.127", {"start": v(98, 1) * mm, "end": v(98, -1) * mm});
            skLineSegment(sketch, "E7.3.0.128", {"start": v(92, 11.55) * mm, "end": v(92, 9.55) * mm});
            skLineSegment(sketch, "E7.3.0.129", {"start": v(82, -4.28) * mm, "end": v(82, -6.28) * mm});
            skLineSegment(sketch, "E7.3.0.130", {"start": v(108, -4.28) * mm, "end": v(112, -4.28) * mm});
            skLineSegment(sketch, "E7.3.0.131", {"start": v(112, 9.55) * mm, "end": v(112, 4.27) * mm, "construction": true});
            skLineSegment(sketch, "E7.3.0.132", {"start": v(68, 1) * mm, "end": v(68, -1) * mm});
            skLineSegment(sketch, "E7.3.0.133", {"start": v(62, 11.55) * mm, "end": v(62, 9.55) * mm});
            skLineSegment(sketch, "E7.3.0.134", {"start": v(52, -4.28) * mm, "end": v(52, -6.28) * mm});
            skLineSegment(sketch, "E7.3.0.135", {"start": v(78, -4.28) * mm, "end": v(82, -4.28) * mm});
            skLineSegment(sketch, "E7.3.0.136", {"start": v(82, 9.55) * mm, "end": v(82, 4.27) * mm, "construction": true});
            skLineSegment(sketch, "E7.3.0.137", {"start": v(108, -4.28) * mm, "end": v(108, -6.28) * mm});
            skLineSegment(sketch, "E7.3.0.138", {"start": v(38, 1) * mm, "end": v(42, 1) * mm});
            skLineSegment(sketch, "E7.3.0.139", {"start": v(18, -9.55) * mm, "end": v(18, -11.55) * mm});
            skLineSegment(sketch, "E7.3.0.140", {"start": v(78, -4.28) * mm, "end": v(78, -6.28) * mm});
            skLineSegment(sketch, "E7.3.0.141", {"start": v(18, -11.55) * mm, "end": v(28, -11.55) * mm, "construction": true});
            skLineSegment(sketch, "E7.3.0.142", {"start": v(32, 11.55) * mm, "end": v(32, 9.55) * mm});
            skLineSegment(sketch, "E7.3.0.143", {"start": v(18, -9.55) * mm, "end": v(22, -9.55) * mm});
            skLineSegment(sketch, "E7.3.0.144", {"start": v(58, 11.55) * mm, "end": v(58, 9.55) * mm});
            skLineSegment(sketch, "E7.3.0.145", {"start": v(48, -4.28) * mm, "end": v(52, -4.28) * mm});
            skLineSegment(sketch, "E7.3.0.146", {"start": v(52, 9.55) * mm, "end": v(52, 4.27) * mm, "construction": true});
            skLineSegment(sketch, "E7.3.0.147", {"start": v(38, 4.27) * mm, "end": v(42, 4.27) * mm});
            skLineSegment(sketch, "E7.3.0.148", {"start": v(28, 11.55) * mm, "end": v(28, 9.55) * mm});
            skLineSegment(sketch, "E7.3.0.149", {"start": v(22, -9.55) * mm, "end": v(22, -11.55) * mm});
            skLineSegment(sketch, "E7.3.0.150", {"start": v(58, 9.55) * mm, "end": v(62, 9.55) * mm});
            skLineSegment(sketch, "E7.3.0.151", {"start": v(48, -4.28) * mm, "end": v(48, -6.28) * mm});
            skLineSegment(sketch, "E7.3.0.152", {"start": v(48, -1) * mm, "end": v(52, -1) * mm});
            skLineSegment(sketch, "E7.3.0.153", {"start": v(88, -6.28) * mm, "end": v(92, -6.28) * mm});
            skLineSegment(sketch, "E7.3.0.154", {"start": v(88, -9.55) * mm, "end": v(88, -11.55) * mm});
            skLineSegment(sketch, "E7.3.0.155", {"start": v(18, -4.28) * mm, "end": v(18, -6.28) * mm});
            skLineSegment(sketch, "E7.3.0.156", {"start": v(18, -4.28) * mm, "end": v(22, -4.28) * mm});
            skLineSegment(sketch, "E7.3.0.157", {"start": v(22, -4.28) * mm, "end": v(22, -6.28) * mm});
            skLineSegment(sketch, "E7.3.0.158", {"start": v(22, 6.27) * mm, "end": v(22, 4.27) * mm});
            skLineSegment(sketch, "E7.3.0.159", {"start": v(18, 1) * mm, "end": v(18, -1) * mm});
            skLineSegment(sketch, "E7.3.0.160", {"start": v(18, 1) * mm, "end": v(22, 1) * mm});
            skLineSegment(sketch, "E7.3.0.161", {"start": v(28, 9.55) * mm, "end": v(32, 9.55) * mm});
            skLineSegment(sketch, "E7.3.0.162", {"start": v(18, -11.55) * mm, "end": v(22, -11.55) * mm});
            skLineSegment(sketch, "E7.3.0.163", {"start": v(18, -1) * mm, "end": v(22, -1) * mm});
            skLineSegment(sketch, "E7.3.0.164", {"start": v(58, -6.28) * mm, "end": v(62, -6.28) * mm});
            skLineSegment(sketch, "E7.3.0.165", {"start": v(58, -9.55) * mm, "end": v(58, -11.55) * mm});
            skLineSegment(sketch, "E7.3.0.166", {"start": v(92, -9.55) * mm, "end": v(92, -11.55) * mm});
            skLineSegment(sketch, "E7.3.0.167", {"start": v(38, 6.27) * mm, "end": v(42, 6.27) * mm});
            skLineSegment(sketch, "E7.3.0.168", {"start": v(28, -6.28) * mm, "end": v(32, -6.28) * mm});
            skLineSegment(sketch, "E7.3.0.169", {"start": v(28, -9.55) * mm, "end": v(28, -11.55) * mm});
            skLineSegment(sketch, "E7.3.0.170", {"start": v(58, 11.55) * mm, "end": v(62, 11.55) * mm});
            skLineSegment(sketch, "E7.3.0.171", {"start": v(62, -9.55) * mm, "end": v(62, -11.55) * mm});
            skLineSegment(sketch, "E7.3.0.172", {"start": v(52, 1) * mm, "end": v(52, -1) * mm});
            skLineSegment(sketch, "E7.3.0.173", {"start": v(88, -9.55) * mm, "end": v(92, -9.55) * mm});
            skLineSegment(sketch, "E7.3.0.174", {"start": v(92, 9.55) * mm, "end": v(92, 4.27) * mm, "construction": true});
            skLineSegment(sketch, "E7.3.0.175", {"start": v(78, 1) * mm, "end": v(78, -1) * mm});
            skLineSegment(sketch, "E7.3.0.176", {"start": v(58, -4.28) * mm, "end": v(58, -6.28) * mm});
            skLineSegment(sketch, "E7.3.0.177", {"start": v(28, -1) * mm, "end": v(32, -1) * mm});
            skLineSegment(sketch, "E7.3.0.178", {"start": v(28, -4.28) * mm, "end": v(28, -6.28) * mm});
            skLineSegment(sketch, "E7.3.0.179", {"start": v(32, 1) * mm, "end": v(32, -1) * mm});
            skLineSegment(sketch, "E7.3.0.180", {"start": v(102, 9.55) * mm, "end": v(102, 4.27) * mm, "construction": true});
            skLineSegment(sketch, "E7.3.0.181", {"start": v(42, 9.55) * mm, "end": v(42, 4.27) * mm, "construction": true});
            skLineSegment(sketch, "E7.3.0.182", {"start": v(28, 1) * mm, "end": v(28, -1) * mm});
            skLineSegment(sketch, "E7.3.0.183", {"start": v(92, 6.27) * mm, "end": v(92, 4.27) * mm});
            skLineSegment(sketch, "E7.3.0.184", {"start": v(68, -4.28) * mm, "end": v(68, -6.28) * mm});
            skLineSegment(sketch, "E7.3.0.185", {"start": v(28, 1) * mm, "end": v(32, 1) * mm});
            skLineSegment(sketch, "E7.3.0.186", {"start": v(58, 1) * mm, "end": v(58, -1) * mm});
            skLineSegment(sketch, "E7.3.0.187", {"start": v(42, -4.28) * mm, "end": v(42, -6.28) * mm});
            skLineSegment(sketch, "E7.3.0.188", {"start": v(72, 9.55) * mm, "end": v(72, 4.27) * mm, "construction": true});
            skLineSegment(sketch, "E7.3.0.189", {"start": v(98, -4.28) * mm, "end": v(98, -6.28) * mm});
            skLineSegment(sketch, "E7.3.0.190", {"start": v(98, 4.27) * mm, "end": v(102, 4.27) * mm});
            skLineSegment(sketch, "E7.3.0.191", {"start": v(108, -1) * mm, "end": v(112, -1) * mm});
            skLineSegment(sketch, "E7.3.0.192", {"start": v(102, 6.27) * mm, "end": v(102, 4.27) * mm});
            skLineSegment(sketch, "E7.3.0.193", {"start": v(78, -1) * mm, "end": v(82, -1) * mm});
            skLineSegment(sketch, "E7.3.0.194", {"start": v(68, 4.27) * mm, "end": v(72, 4.27) * mm});
            skLineSegment(sketch, "E7.3.0.195", {"start": v(112, 1) * mm, "end": v(112, -1) * mm});
            skLineSegment(sketch, "E7.3.0.196", {"start": v(72, 6.27) * mm, "end": v(72, 4.27) * mm});
            skLineSegment(sketch, "E7.3.0.197", {"start": v(98, 6.27) * mm, "end": v(102, 6.27) * mm});
            skLineSegment(sketch, "E7.3.0.198", {"start": v(22, 11.55) * mm, "end": v(22, 9.55) * mm});
            skLineSegment(sketch, "E7.3.0.199", {"start": v(22, 1) * mm, "end": v(22, -1) * mm});
            skLineSegment(sketch, "E7.3.0.200", {"start": v(42, 6.27) * mm, "end": v(42, 4.27) * mm});
            skLineSegment(sketch, "E7.3.0.201", {"start": v(68, 6.27) * mm, "end": v(72, 6.27) * mm});
            skLineSegment(sketch, "E7.3.0.202", {"start": v(22, 9.55) * mm, "end": v(22, 4.27) * mm, "construction": true});
            skLineSegment(sketch, "E7.3.0.203", {"start": v(98, 6.27) * mm, "end": v(98, 4.27) * mm});
            skLineSegment(sketch, "E7.3.0.204", {"start": v(82, 1) * mm, "end": v(82, -1) * mm});
            skLineSegment(sketch, "E7.3.0.205", {"start": v(108, 1) * mm, "end": v(112, 1) * mm});
            skLineSegment(sketch, "E7.3.0.206", {"start": v(68, 6.27) * mm, "end": v(68, 4.27) * mm});
            skLineSegment(sketch, "E7.3.0.207", {"start": v(102, 11.55) * mm, "end": v(102, 9.55) * mm});
            skLineSegment(sketch, "E7.3.0.208", {"start": v(92, -4.28) * mm, "end": v(92, -6.28) * mm});
            skLineSegment(sketch, "E7.3.0.209", {"start": v(78, 1) * mm, "end": v(82, 1) * mm});
            skLineSegment(sketch, "E7.3.0.210", {"start": v(108, 1) * mm, "end": v(108, -1) * mm});
            skLineSegment(sketch, "E7.4.0.0", {"start": v(128, -9.55) * mm, "end": v(132, -9.55) * mm});
            skLineSegment(sketch, "E7.4.0.1", {"start": v(132, -9.55) * mm, "end": v(132, -11.55) * mm});
            skLineSegment(sketch, "E7.4.0.2", {"start": v(198, 11.55) * mm, "end": v(198, 9.55) * mm});
            skLineSegment(sketch, "E7.4.0.3", {"start": v(188, -1) * mm, "end": v(192, -1) * mm});
            skLineSegment(sketch, "E7.4.0.4", {"start": v(168, 11.55) * mm, "end": v(168, 9.55) * mm});
            skLineSegment(sketch, "E7.4.0.5", {"start": v(198, 9.55) * mm, "end": v(202, 9.55) * mm});
            skLineSegment(sketch, "E7.4.0.6", {"start": v(138, 11.55) * mm, "end": v(138, 9.55) * mm});
            skLineSegment(sketch, "E7.4.0.7", {"start": v(168, 9.55) * mm, "end": v(172, 9.55) * mm});
            skLineSegment(sketch, "E7.4.0.8", {"start": v(198, -9.55) * mm, "end": v(198, -11.55) * mm});
            skLineSegment(sketch, "E7.4.0.9", {"start": v(138, 9.55) * mm, "end": v(142, 9.55) * mm});
            skLineSegment(sketch, "E7.4.0.10", {"start": v(192, 1) * mm, "end": v(192, -1) * mm});
            skLineSegment(sketch, "E7.4.0.11", {"start": v(208, 6.27) * mm, "end": v(208, 4.27) * mm});
            skLineSegment(sketch, "E7.4.0.12", {"start": v(198, 11.55) * mm, "end": v(202, 11.55) * mm});
            skLineSegment(sketch, "E7.4.0.13", {"start": v(202, -9.55) * mm, "end": v(202, -11.55) * mm});
            skLineSegment(sketch, "E7.4.0.14", {"start": v(128, -11.55) * mm, "end": v(132, -11.55) * mm});
            skLineSegment(sketch, "E7.4.0.15", {"start": v(188, 1) * mm, "end": v(192, 1) * mm});
            skLineSegment(sketch, "E7.4.0.16", {"start": v(168, 11.55) * mm, "end": v(172, 11.55) * mm});
            skLineSegment(sketch, "E7.4.0.17", {"start": v(172, -9.55) * mm, "end": v(172, -11.55) * mm});
            skLineSegment(sketch, "E7.4.0.18", {"start": v(198, -9.55) * mm, "end": v(202, -9.55) * mm});
            skLineSegment(sketch, "E7.4.0.19", {"start": v(138, 11.55) * mm, "end": v(142, 11.55) * mm});
            skLineSegment(sketch, "E7.4.0.20", {"start": v(168, -9.55) * mm, "end": v(172, -9.55) * mm});
            skLineSegment(sketch, "E7.4.0.21", {"start": v(168, -1) * mm, "end": v(172, -1) * mm});
            skLineSegment(sketch, "E7.4.0.22", {"start": v(198, -11.55) * mm, "end": v(202, -11.55) * mm});
            skLineSegment(sketch, "E7.4.0.23", {"start": v(138, -1) * mm, "end": v(142, -1) * mm});
            skLineSegment(sketch, "E7.4.0.24", {"start": v(168, -11.55) * mm, "end": v(172, -11.55) * mm});
            skLineSegment(sketch, "E7.4.0.25", {"start": v(178, -9.55) * mm, "end": v(178, -11.55) * mm});
            skLineSegment(sketch, "E7.4.0.26", {"start": v(212, -9.55) * mm, "end": v(212, -11.55) * mm});
            skLineSegment(sketch, "E7.4.0.27", {"start": v(172, 1) * mm, "end": v(172, -1) * mm});
            skLineSegment(sketch, "E7.4.0.28", {"start": v(148, -9.55) * mm, "end": v(148, -11.55) * mm});
            skLineSegment(sketch, "E7.4.0.29", {"start": v(182, -9.55) * mm, "end": v(182, -11.55) * mm});
            skLineSegment(sketch, "E7.4.0.30", {"start": v(208, -9.55) * mm, "end": v(212, -9.55) * mm});
            skLineSegment(sketch, "E7.4.0.31", {"start": v(168, 1) * mm, "end": v(172, 1) * mm});
            skLineSegment(sketch, "E7.4.0.32", {"start": v(152, -9.55) * mm, "end": v(152, -11.55) * mm});
            skLineSegment(sketch, "E7.4.0.33", {"start": v(178, -9.55) * mm, "end": v(182, -9.55) * mm});
            skLineSegment(sketch, "E7.4.0.34", {"start": v(148, -9.55) * mm, "end": v(152, -9.55) * mm});
            skLineSegment(sketch, "E7.4.0.35", {"start": v(188, 11.55) * mm, "end": v(188, 9.55) * mm});
            skLineSegment(sketch, "E7.4.0.36", {"start": v(128, 6.27) * mm, "end": v(128, 4.27) * mm});
            skLineSegment(sketch, "E7.4.0.37", {"start": v(188, 9.55) * mm, "end": v(192, 9.55) * mm});
            skLineSegment(sketch, "E7.4.0.38", {"start": v(208, -11.55) * mm, "end": v(212, -11.55) * mm});
            skLineSegment(sketch, "E7.4.0.39", {"start": v(138, 1) * mm, "end": v(138, -1) * mm});
            skLineSegment(sketch, "E7.4.0.40", {"start": v(178, -11.55) * mm, "end": v(182, -11.55) * mm});
            skLineSegment(sketch, "E7.4.0.41", {"start": v(118, 11.55) * mm, "end": v(122, 11.55) * mm});
            skLineSegment(sketch, "E7.4.0.42", {"start": v(118, 9.55) * mm, "end": v(122, 9.55) * mm});
            skLineSegment(sketch, "E7.4.0.43", {"start": v(118, 11.55) * mm, "end": v(118, 9.55) * mm});
            skLineSegment(sketch, "E7.4.0.44", {"start": v(118, 6.27) * mm, "end": v(118, 4.27) * mm});
            skLineSegment(sketch, "E7.4.0.45", {"start": v(118, 6.27) * mm, "end": v(122, 6.27) * mm});
            skLineSegment(sketch, "E7.4.0.46", {"start": v(118, 4.27) * mm, "end": v(122, 4.27) * mm});
            skLineSegment(sketch, "E7.4.0.47", {"start": v(148, -11.55) * mm, "end": v(152, -11.55) * mm});
            skLineSegment(sketch, "E7.4.0.48", {"start": v(188, 11.55) * mm, "end": v(192, 11.55) * mm});
            skLineSegment(sketch, "E7.4.0.49", {"start": v(138, 6.27) * mm, "end": v(138, 4.27) * mm});
            skLineSegment(sketch, "E7.4.0.50", {"start": v(128, 11.55) * mm, "end": v(132, 11.55) * mm});
            skLineSegment(sketch, "E7.4.0.51", {"start": v(172, 11.55) * mm, "end": v(172, 9.55) * mm});
            skLineSegment(sketch, "E7.4.0.52", {"start": v(162, -4.28) * mm, "end": v(162, -6.28) * mm});
            skLineSegment(sketch, "E7.4.0.53", {"start": v(158, -9.55) * mm, "end": v(162, -9.55) * mm});
            skLineSegment(sketch, "E7.4.0.54", {"start": v(148, 1) * mm, "end": v(152, 1) * mm});
            skLineSegment(sketch, "E7.4.0.55", {"start": v(188, -4.28) * mm, "end": v(192, -4.28) * mm});
            skLineSegment(sketch, "E7.4.0.56", {"start": v(208, 4.27) * mm, "end": v(212, 4.27) * mm});
            skLineSegment(sketch, "E7.4.0.57", {"start": v(162, 9.55) * mm, "end": v(162, 4.27) * mm, "construction": true});
            skLineSegment(sketch, "E7.4.0.58", {"start": v(148, 1) * mm, "end": v(148, -1) * mm});
            skLineSegment(sketch, "E7.4.0.59", {"start": v(142, 11.55) * mm, "end": v(142, 9.55) * mm});
            skLineSegment(sketch, "E7.4.0.60", {"start": v(132, -4.28) * mm, "end": v(132, -6.28) * mm});
            skLineSegment(sketch, "E7.4.0.61", {"start": v(178, 4.27) * mm, "end": v(182, 4.27) * mm});
            skLineSegment(sketch, "E7.4.0.62", {"start": v(158, -4.28) * mm, "end": v(162, -4.28) * mm});
            skLineSegment(sketch, "E7.4.0.63", {"start": v(212, 6.27) * mm, "end": v(212, 4.27) * mm});
            skLineSegment(sketch, "E7.4.0.64", {"start": v(188, -4.28) * mm, "end": v(188, -6.28) * mm});
            skLineSegment(sketch, "E7.4.0.65", {"start": v(132, 9.55) * mm, "end": v(132, 4.27) * mm, "construction": true});
            skLineSegment(sketch, "E7.4.0.66", {"start": v(158, -1) * mm, "end": v(162, -1) * mm});
            skLineSegment(sketch, "E7.4.0.67", {"start": v(148, 4.27) * mm, "end": v(152, 4.27) * mm});
            skLineSegment(sketch, "E7.4.0.68", {"start": v(128, -4.28) * mm, "end": v(132, -4.28) * mm});
            skLineSegment(sketch, "E7.4.0.69", {"start": v(188, -11.55) * mm, "end": v(192, -11.55) * mm});
            skLineSegment(sketch, "E7.4.0.70", {"start": v(182, 6.27) * mm, "end": v(182, 4.27) * mm});
            skLineSegment(sketch, "E7.4.0.71", {"start": v(208, 6.27) * mm, "end": v(212, 6.27) * mm});
            skLineSegment(sketch, "E7.4.0.72", {"start": v(198, -6.28) * mm, "end": v(202, -6.28) * mm});
            skLineSegment(sketch, "E7.4.0.73", {"start": v(158, -11.55) * mm, "end": v(162, -11.55) * mm});
            skLineSegment(sketch, "E7.4.0.74", {"start": v(152, 6.27) * mm, "end": v(152, 4.27) * mm});
            skLineSegment(sketch, "E7.4.0.75", {"start": v(178, 6.27) * mm, "end": v(182, 6.27) * mm});
            skLineSegment(sketch, "E7.4.0.76", {"start": v(168, -6.28) * mm, "end": v(172, -6.28) * mm});
            skLineSegment(sketch, "E7.4.0.77", {"start": v(168, -9.55) * mm, "end": v(168, -11.55) * mm});
            skLineSegment(sketch, "E7.4.0.78", {"start": v(162, 1) * mm, "end": v(162, -1) * mm});
            skLineSegment(sketch, "E7.4.0.79", {"start": v(148, 6.27) * mm, "end": v(152, 6.27) * mm});
            skLineSegment(sketch, "E7.4.0.80", {"start": v(138, -6.28) * mm, "end": v(142, -6.28) * mm});
            skLineSegment(sketch, "E7.4.0.81", {"start": v(138, -9.55) * mm, "end": v(138, -11.55) * mm});
            skLineSegment(sketch, "E7.4.0.82", {"start": v(178, 6.27) * mm, "end": v(178, 4.27) * mm});
            skLineSegment(sketch, "E7.4.0.83", {"start": v(212, 11.55) * mm, "end": v(212, 9.55) * mm});
            skLineSegment(sketch, "E7.4.0.84", {"start": v(202, -4.28) * mm, "end": v(202, -6.28) * mm});
            skLineSegment(sketch, "E7.4.0.85", {"start": v(158, 1) * mm, "end": v(162, 1) * mm});
            skLineSegment(sketch, "E7.4.0.86", {"start": v(148, 6.27) * mm, "end": v(148, 4.27) * mm});
            skLineSegment(sketch, "E7.4.0.87", {"start": v(142, -9.55) * mm, "end": v(142, -11.55) * mm});
            skLineSegment(sketch, "E7.4.0.88", {"start": v(188, 1) * mm, "end": v(188, -1) * mm});
            skLineSegment(sketch, "E7.4.0.89", {"start": v(182, 11.55) * mm, "end": v(182, 9.55) * mm});
            skLineSegment(sketch, "E7.4.0.90", {"start": v(172, -4.28) * mm, "end": v(172, -6.28) * mm});
            skLineSegment(sketch, "E7.4.0.91", {"start": v(208, 11.55) * mm, "end": v(208, 9.55) * mm});
            skLineSegment(sketch, "E7.4.0.92", {"start": v(198, -4.28) * mm, "end": v(202, -4.28) * mm});
            skLineSegment(sketch, "E7.4.0.93", {"start": v(158, 4.27) * mm, "end": v(162, 4.27) * mm});
            skLineSegment(sketch, "E7.4.0.94", {"start": v(148, 11.55) * mm, "end": v(148, 9.55) * mm});
            skLineSegment(sketch, "E7.4.0.95", {"start": v(138, -4.28) * mm, "end": v(142, -4.28) * mm});
            skLineSegment(sketch, "E7.4.0.96", {"start": v(178, 9.55) * mm, "end": v(182, 9.55) * mm});
            skLineSegment(sketch, "E7.4.0.97", {"start": v(208, -6.28) * mm, "end": v(212, -6.28) * mm});
            skLineSegment(sketch, "E7.4.0.98", {"start": v(208, -9.55) * mm, "end": v(208, -11.55) * mm});
            skLineSegment(sketch, "E7.4.0.99", {"start": v(152, 11.55) * mm, "end": v(152, 9.55) * mm});
            skLineSegment(sketch, "E7.4.0.100", {"start": v(138, -9.55) * mm, "end": v(142, -9.55) * mm});
            skLineSegment(sketch, "E7.4.0.101", {"start": v(188, 4.27) * mm, "end": v(192, 4.27) * mm});
            skLineSegment(sketch, "E7.4.0.102", {"start": v(178, 11.55) * mm, "end": v(178, 9.55) * mm});
            skLineSegment(sketch, "E7.4.0.103", {"start": v(168, -4.28) * mm, "end": v(172, -4.28) * mm});
            skLineSegment(sketch, "E7.4.0.104", {"start": v(208, 9.55) * mm, "end": v(212, 9.55) * mm});
            skLineSegment(sketch, "E7.4.0.105", {"start": v(198, -1) * mm, "end": v(202, -1) * mm});
            skLineSegment(sketch, "E7.4.0.106", {"start": v(128, 4.27) * mm, "end": v(132, 4.27) * mm});
            skLineSegment(sketch, "E7.4.0.107", {"start": v(162, 6.27) * mm, "end": v(162, 4.27) * mm});
            skLineSegment(sketch, "E7.4.0.108", {"start": v(148, 9.55) * mm, "end": v(152, 9.55) * mm});
            skLineSegment(sketch, "E7.4.0.109", {"start": v(138, -4.28) * mm, "end": v(138, -6.28) * mm});
            skLineSegment(sketch, "E7.4.0.110", {"start": v(202, 1) * mm, "end": v(202, -1) * mm});
            skLineSegment(sketch, "E7.4.0.111", {"start": v(188, 6.27) * mm, "end": v(192, 6.27) * mm});
            skLineSegment(sketch, "E7.4.0.112", {"start": v(178, -6.28) * mm, "end": v(182, -6.28) * mm});
            skLineSegment(sketch, "E7.4.0.113", {"start": v(208, 11.55) * mm, "end": v(212, 11.55) * mm});
            skLineSegment(sketch, "E7.4.0.114", {"start": v(138, -11.55) * mm, "end": v(142, -11.55) * mm});
            skLineSegment(sketch, "E7.4.0.115", {"start": v(132, 6.27) * mm, "end": v(132, 4.27) * mm});
            skLineSegment(sketch, "E7.4.0.116", {"start": v(158, 6.27) * mm, "end": v(162, 6.27) * mm});
            skLineSegment(sketch, "E7.4.0.117", {"start": v(148, -6.28) * mm, "end": v(152, -6.28) * mm});
            skLineSegment(sketch, "E7.4.0.118", {"start": v(198, 1) * mm, "end": v(202, 1) * mm});
            skLineSegment(sketch, "E7.4.0.119", {"start": v(188, 6.27) * mm, "end": v(188, 4.27) * mm});
            skLineSegment(sketch, "E7.4.0.120", {"start": v(178, 11.55) * mm, "end": v(182, 11.55) * mm});
            skLineSegment(sketch, "E7.4.0.121", {"start": v(212, -4.28) * mm, "end": v(212, -6.28) * mm});
            skLineSegment(sketch, "E7.4.0.122", {"start": v(142, 1) * mm, "end": v(142, -1) * mm});
            skLineSegment(sketch, "E7.4.0.123", {"start": v(128, 6.27) * mm, "end": v(132, 6.27) * mm});
            skLineSegment(sketch, "E7.4.0.124", {"start": v(118, -6.28) * mm, "end": v(122, -6.28) * mm});
            skLineSegment(sketch, "E7.4.0.125", {"start": v(158, 6.27) * mm, "end": v(158, 4.27) * mm});
            skLineSegment(sketch, "E7.4.0.126", {"start": v(148, 11.55) * mm, "end": v(152, 11.55) * mm});
            skLineSegment(sketch, "E7.4.0.127", {"start": v(198, 1) * mm, "end": v(198, -1) * mm});
            skLineSegment(sketch, "E7.4.0.128", {"start": v(192, 11.55) * mm, "end": v(192, 9.55) * mm});
            skLineSegment(sketch, "E7.4.0.129", {"start": v(182, -4.28) * mm, "end": v(182, -6.28) * mm});
            skLineSegment(sketch, "E7.4.0.130", {"start": v(208, -4.28) * mm, "end": v(212, -4.28) * mm});
            skLineSegment(sketch, "E7.4.0.131", {"start": v(212, 9.55) * mm, "end": v(212, 4.27) * mm, "construction": true});
            skLineSegment(sketch, "E7.4.0.132", {"start": v(168, 1) * mm, "end": v(168, -1) * mm});
            skLineSegment(sketch, "E7.4.0.133", {"start": v(162, 11.55) * mm, "end": v(162, 9.55) * mm});
            skLineSegment(sketch, "E7.4.0.134", {"start": v(152, -4.28) * mm, "end": v(152, -6.28) * mm});
            skLineSegment(sketch, "E7.4.0.135", {"start": v(178, -4.28) * mm, "end": v(182, -4.28) * mm});
            skLineSegment(sketch, "E7.4.0.136", {"start": v(182, 9.55) * mm, "end": v(182, 4.27) * mm, "construction": true});
            skLineSegment(sketch, "E7.4.0.137", {"start": v(208, -4.28) * mm, "end": v(208, -6.28) * mm});
            skLineSegment(sketch, "E7.4.0.138", {"start": v(138, 1) * mm, "end": v(142, 1) * mm});
            skLineSegment(sketch, "E7.4.0.139", {"start": v(118, -9.55) * mm, "end": v(118, -11.55) * mm});
            skLineSegment(sketch, "E7.4.0.140", {"start": v(178, -4.28) * mm, "end": v(178, -6.28) * mm});
            skLineSegment(sketch, "E7.4.0.141", {"start": v(118, -11.55) * mm, "end": v(128, -11.55) * mm, "construction": true});
            skLineSegment(sketch, "E7.4.0.142", {"start": v(132, 11.55) * mm, "end": v(132, 9.55) * mm});
            skLineSegment(sketch, "E7.4.0.143", {"start": v(118, -9.55) * mm, "end": v(122, -9.55) * mm});
            skLineSegment(sketch, "E7.4.0.144", {"start": v(158, 11.55) * mm, "end": v(158, 9.55) * mm});
            skLineSegment(sketch, "E7.4.0.145", {"start": v(148, -4.28) * mm, "end": v(152, -4.28) * mm});
            skLineSegment(sketch, "E7.4.0.146", {"start": v(152, 9.55) * mm, "end": v(152, 4.27) * mm, "construction": true});
            skLineSegment(sketch, "E7.4.0.147", {"start": v(138, 4.27) * mm, "end": v(142, 4.27) * mm});
            skLineSegment(sketch, "E7.4.0.148", {"start": v(128, 11.55) * mm, "end": v(128, 9.55) * mm});
            skLineSegment(sketch, "E7.4.0.149", {"start": v(122, -9.55) * mm, "end": v(122, -11.55) * mm});
            skLineSegment(sketch, "E7.4.0.150", {"start": v(158, 9.55) * mm, "end": v(162, 9.55) * mm});
            skLineSegment(sketch, "E7.4.0.151", {"start": v(148, -4.28) * mm, "end": v(148, -6.28) * mm});
            skLineSegment(sketch, "E7.4.0.152", {"start": v(148, -1) * mm, "end": v(152, -1) * mm});
            skLineSegment(sketch, "E7.4.0.153", {"start": v(188, -6.28) * mm, "end": v(192, -6.28) * mm});
            skLineSegment(sketch, "E7.4.0.154", {"start": v(188, -9.55) * mm, "end": v(188, -11.55) * mm});
            skLineSegment(sketch, "E7.4.0.155", {"start": v(118, -4.28) * mm, "end": v(118, -6.28) * mm});
            skLineSegment(sketch, "E7.4.0.156", {"start": v(118, -4.28) * mm, "end": v(122, -4.28) * mm});
            skLineSegment(sketch, "E7.4.0.157", {"start": v(122, -4.28) * mm, "end": v(122, -6.28) * mm});
            skLineSegment(sketch, "E7.4.0.158", {"start": v(122, 6.27) * mm, "end": v(122, 4.27) * mm});
            skLineSegment(sketch, "E7.4.0.159", {"start": v(118, 1) * mm, "end": v(118, -1) * mm});
            skLineSegment(sketch, "E7.4.0.160", {"start": v(118, 1) * mm, "end": v(122, 1) * mm});
            skLineSegment(sketch, "E7.4.0.161", {"start": v(128, 9.55) * mm, "end": v(132, 9.55) * mm});
            skLineSegment(sketch, "E7.4.0.162", {"start": v(118, -11.55) * mm, "end": v(122, -11.55) * mm});
            skLineSegment(sketch, "E7.4.0.163", {"start": v(118, -1) * mm, "end": v(122, -1) * mm});
            skLineSegment(sketch, "E7.4.0.164", {"start": v(158, -6.28) * mm, "end": v(162, -6.28) * mm});
            skLineSegment(sketch, "E7.4.0.165", {"start": v(158, -9.55) * mm, "end": v(158, -11.55) * mm});
            skLineSegment(sketch, "E7.4.0.166", {"start": v(192, -9.55) * mm, "end": v(192, -11.55) * mm});
            skLineSegment(sketch, "E7.4.0.167", {"start": v(138, 6.27) * mm, "end": v(142, 6.27) * mm});
            skLineSegment(sketch, "E7.4.0.168", {"start": v(128, -6.28) * mm, "end": v(132, -6.28) * mm});
            skLineSegment(sketch, "E7.4.0.169", {"start": v(128, -9.55) * mm, "end": v(128, -11.55) * mm});
            skLineSegment(sketch, "E7.4.0.170", {"start": v(158, 11.55) * mm, "end": v(162, 11.55) * mm});
            skLineSegment(sketch, "E7.4.0.171", {"start": v(162, -9.55) * mm, "end": v(162, -11.55) * mm});
            skLineSegment(sketch, "E7.4.0.172", {"start": v(152, 1) * mm, "end": v(152, -1) * mm});
            skLineSegment(sketch, "E7.4.0.173", {"start": v(188, -9.55) * mm, "end": v(192, -9.55) * mm});
            skLineSegment(sketch, "E7.4.0.174", {"start": v(192, 9.55) * mm, "end": v(192, 4.27) * mm, "construction": true});
            skLineSegment(sketch, "E7.4.0.175", {"start": v(178, 1) * mm, "end": v(178, -1) * mm});
            skLineSegment(sketch, "E7.4.0.176", {"start": v(158, -4.28) * mm, "end": v(158, -6.28) * mm});
            skLineSegment(sketch, "E7.4.0.177", {"start": v(128, -1) * mm, "end": v(132, -1) * mm});
            skLineSegment(sketch, "E7.4.0.178", {"start": v(128, -4.28) * mm, "end": v(128, -6.28) * mm});
            skLineSegment(sketch, "E7.4.0.179", {"start": v(132, 1) * mm, "end": v(132, -1) * mm});
            skLineSegment(sketch, "E7.4.0.180", {"start": v(202, 9.55) * mm, "end": v(202, 4.27) * mm, "construction": true});
            skLineSegment(sketch, "E7.4.0.181", {"start": v(142, 9.55) * mm, "end": v(142, 4.27) * mm, "construction": true});
            skLineSegment(sketch, "E7.4.0.182", {"start": v(128, 1) * mm, "end": v(128, -1) * mm});
            skLineSegment(sketch, "E7.4.0.183", {"start": v(192, 6.27) * mm, "end": v(192, 4.27) * mm});
            skLineSegment(sketch, "E7.4.0.184", {"start": v(168, -4.28) * mm, "end": v(168, -6.28) * mm});
            skLineSegment(sketch, "E7.4.0.185", {"start": v(128, 1) * mm, "end": v(132, 1) * mm});
            skLineSegment(sketch, "E7.4.0.186", {"start": v(158, 1) * mm, "end": v(158, -1) * mm});
            skLineSegment(sketch, "E7.4.0.187", {"start": v(142, -4.28) * mm, "end": v(142, -6.28) * mm});
            skLineSegment(sketch, "E7.4.0.188", {"start": v(172, 9.55) * mm, "end": v(172, 4.27) * mm, "construction": true});
            skLineSegment(sketch, "E7.4.0.189", {"start": v(198, -4.28) * mm, "end": v(198, -6.28) * mm});
            skLineSegment(sketch, "E7.4.0.190", {"start": v(198, 4.27) * mm, "end": v(202, 4.27) * mm});
            skLineSegment(sketch, "E7.4.0.191", {"start": v(208, -1) * mm, "end": v(212, -1) * mm});
            skLineSegment(sketch, "E7.4.0.192", {"start": v(202, 6.27) * mm, "end": v(202, 4.27) * mm});
            skLineSegment(sketch, "E7.4.0.193", {"start": v(178, -1) * mm, "end": v(182, -1) * mm});
            skLineSegment(sketch, "E7.4.0.194", {"start": v(168, 4.27) * mm, "end": v(172, 4.27) * mm});
            skLineSegment(sketch, "E7.4.0.195", {"start": v(212, 1) * mm, "end": v(212, -1) * mm});
            skLineSegment(sketch, "E7.4.0.196", {"start": v(172, 6.27) * mm, "end": v(172, 4.27) * mm});
            skLineSegment(sketch, "E7.4.0.197", {"start": v(198, 6.27) * mm, "end": v(202, 6.27) * mm});
            skLineSegment(sketch, "E7.4.0.198", {"start": v(122, 11.55) * mm, "end": v(122, 9.55) * mm});
            skLineSegment(sketch, "E7.4.0.199", {"start": v(122, 1) * mm, "end": v(122, -1) * mm});
            skLineSegment(sketch, "E7.4.0.200", {"start": v(142, 6.27) * mm, "end": v(142, 4.27) * mm});
            skLineSegment(sketch, "E7.4.0.201", {"start": v(168, 6.27) * mm, "end": v(172, 6.27) * mm});
            skLineSegment(sketch, "E7.4.0.202", {"start": v(122, 9.55) * mm, "end": v(122, 4.27) * mm, "construction": true});
            skLineSegment(sketch, "E7.4.0.203", {"start": v(198, 6.27) * mm, "end": v(198, 4.27) * mm});
            skLineSegment(sketch, "E7.4.0.204", {"start": v(182, 1) * mm, "end": v(182, -1) * mm});
            skLineSegment(sketch, "E7.4.0.205", {"start": v(208, 1) * mm, "end": v(212, 1) * mm});
            skLineSegment(sketch, "E7.4.0.206", {"start": v(168, 6.27) * mm, "end": v(168, 4.27) * mm});
            skLineSegment(sketch, "E7.4.0.207", {"start": v(202, 11.55) * mm, "end": v(202, 9.55) * mm});
            skLineSegment(sketch, "E7.4.0.208", {"start": v(192, -4.28) * mm, "end": v(192, -6.28) * mm});
            skLineSegment(sketch, "E7.4.0.209", {"start": v(178, 1) * mm, "end": v(182, 1) * mm});
            skLineSegment(sketch, "E7.4.0.210", {"start": v(208, 1) * mm, "end": v(208, -1) * mm});
            skLineSegment(sketch, "E7.5.0.0", {"start": v(228, -9.55) * mm, "end": v(232, -9.55) * mm});
            skLineSegment(sketch, "E7.5.0.1", {"start": v(232, -9.55) * mm, "end": v(232, -11.55) * mm});
            skLineSegment(sketch, "E7.5.0.4", {"start": v(268, 11.55) * mm, "end": v(268, 9.55) * mm});
            skLineSegment(sketch, "E7.5.0.6", {"start": v(238, 11.55) * mm, "end": v(238, 9.55) * mm});
            skLineSegment(sketch, "E7.5.0.7", {"start": v(268, 9.55) * mm, "end": v(272, 9.55) * mm});
            skLineSegment(sketch, "E7.5.0.9", {"start": v(238, 9.55) * mm, "end": v(242, 9.55) * mm});
            skLineSegment(sketch, "E7.5.0.14", {"start": v(228, -11.55) * mm, "end": v(232, -11.55) * mm});
            skLineSegment(sketch, "E7.5.0.16", {"start": v(268, 11.55) * mm, "end": v(272, 11.55) * mm});
            skLineSegment(sketch, "E7.5.0.17", {"start": v(272, -9.55) * mm, "end": v(272, -11.55) * mm});
            skLineSegment(sketch, "E7.5.0.19", {"start": v(238, 11.55) * mm, "end": v(242, 11.55) * mm});
            skLineSegment(sketch, "E7.5.0.20", {"start": v(268, -9.55) * mm, "end": v(272, -9.55) * mm});
            skLineSegment(sketch, "E7.5.0.21", {"start": v(268, -1) * mm, "end": v(272, -1) * mm});
            skLineSegment(sketch, "E7.5.0.23", {"start": v(238, -1) * mm, "end": v(242, -1) * mm});
            skLineSegment(sketch, "E7.5.0.24", {"start": v(268, -11.55) * mm, "end": v(272, -11.55) * mm});
            skLineSegment(sketch, "E7.5.0.25", {"start": v(278, -9.55) * mm, "end": v(278, -11.55) * mm});
            skLineSegment(sketch, "E7.5.0.27", {"start": v(272, 1) * mm, "end": v(272, -1) * mm});
            skLineSegment(sketch, "E7.5.0.28", {"start": v(248, -9.55) * mm, "end": v(248, -11.55) * mm});
            skLineSegment(sketch, "E7.5.0.29", {"start": v(282, -9.55) * mm, "end": v(282, -11.55) * mm});
            skLineSegment(sketch, "E7.5.0.31", {"start": v(268, 1) * mm, "end": v(272, 1) * mm});
            skLineSegment(sketch, "E7.5.0.32", {"start": v(252, -9.55) * mm, "end": v(252, -11.55) * mm});
            skLineSegment(sketch, "E7.5.0.33", {"start": v(278, -9.55) * mm, "end": v(282, -9.55) * mm});
            skLineSegment(sketch, "E7.5.0.34", {"start": v(248, -9.55) * mm, "end": v(252, -9.55) * mm});
            skLineSegment(sketch, "E7.5.0.36", {"start": v(228, 6.27) * mm, "end": v(228, 4.27) * mm});
            skLineSegment(sketch, "E7.5.0.39", {"start": v(238, 1) * mm, "end": v(238, -1) * mm});
            skLineSegment(sketch, "E7.5.0.40", {"start": v(278, -11.55) * mm, "end": v(282, -11.55) * mm});
            skLineSegment(sketch, "E7.5.0.41", {"start": v(218, 11.55) * mm, "end": v(222, 11.55) * mm});
            skLineSegment(sketch, "E7.5.0.42", {"start": v(218, 9.55) * mm, "end": v(222, 9.55) * mm});
            skLineSegment(sketch, "E7.5.0.43", {"start": v(218, 11.55) * mm, "end": v(218, 9.55) * mm});
            skLineSegment(sketch, "E7.5.0.44", {"start": v(218, 6.27) * mm, "end": v(218, 4.27) * mm});
            skLineSegment(sketch, "E7.5.0.45", {"start": v(218, 6.27) * mm, "end": v(222, 6.27) * mm});
            skLineSegment(sketch, "E7.5.0.46", {"start": v(218, 4.27) * mm, "end": v(222, 4.27) * mm});
            skLineSegment(sketch, "E7.5.0.47", {"start": v(248, -11.55) * mm, "end": v(252, -11.55) * mm});
            skLineSegment(sketch, "E7.5.0.49", {"start": v(238, 6.27) * mm, "end": v(238, 4.27) * mm});
            skLineSegment(sketch, "E7.5.0.50", {"start": v(228, 11.55) * mm, "end": v(232, 11.55) * mm});
            skLineSegment(sketch, "E7.5.0.51", {"start": v(272, 11.55) * mm, "end": v(272, 9.55) * mm});
            skLineSegment(sketch, "E7.5.0.52", {"start": v(262, -4.28) * mm, "end": v(262, -6.28) * mm});
            skLineSegment(sketch, "E7.5.0.53", {"start": v(258, -9.55) * mm, "end": v(262, -9.55) * mm});
            skLineSegment(sketch, "E7.5.0.54", {"start": v(248, 1) * mm, "end": v(252, 1) * mm});
            skLineSegment(sketch, "E7.5.0.57", {"start": v(262, 9.55) * mm, "end": v(262, 4.27) * mm, "construction": true});
            skLineSegment(sketch, "E7.5.0.58", {"start": v(248, 1) * mm, "end": v(248, -1) * mm});
            skLineSegment(sketch, "E7.5.0.59", {"start": v(242, 11.55) * mm, "end": v(242, 9.55) * mm});
            skLineSegment(sketch, "E7.5.0.60", {"start": v(232, -4.28) * mm, "end": v(232, -6.28) * mm});
            skLineSegment(sketch, "E7.5.0.61", {"start": v(278, 4.27) * mm, "end": v(282, 4.27) * mm});
            skLineSegment(sketch, "E7.5.0.62", {"start": v(258, -4.28) * mm, "end": v(262, -4.28) * mm});
            skLineSegment(sketch, "E7.5.0.65", {"start": v(232, 9.55) * mm, "end": v(232, 4.27) * mm, "construction": true});
            skLineSegment(sketch, "E7.5.0.66", {"start": v(258, -1) * mm, "end": v(262, -1) * mm});
            skLineSegment(sketch, "E7.5.0.67", {"start": v(248, 4.27) * mm, "end": v(252, 4.27) * mm});
            skLineSegment(sketch, "E7.5.0.68", {"start": v(228, -4.28) * mm, "end": v(232, -4.28) * mm});
            skLineSegment(sketch, "E7.5.0.70", {"start": v(282, 6.27) * mm, "end": v(282, 4.27) * mm});
            skLineSegment(sketch, "E7.5.0.73", {"start": v(258, -11.55) * mm, "end": v(262, -11.55) * mm});
            skLineSegment(sketch, "E7.5.0.74", {"start": v(252, 6.27) * mm, "end": v(252, 4.27) * mm});
            skLineSegment(sketch, "E7.5.0.75", {"start": v(278, 6.27) * mm, "end": v(282, 6.27) * mm});
            skLineSegment(sketch, "E7.5.0.76", {"start": v(268, -6.28) * mm, "end": v(272, -6.28) * mm});
            skLineSegment(sketch, "E7.5.0.77", {"start": v(268, -9.55) * mm, "end": v(268, -11.55) * mm});
            skLineSegment(sketch, "E7.5.0.78", {"start": v(262, 1) * mm, "end": v(262, -1) * mm});
            skLineSegment(sketch, "E7.5.0.79", {"start": v(248, 6.27) * mm, "end": v(252, 6.27) * mm});
            skLineSegment(sketch, "E7.5.0.80", {"start": v(238, -6.28) * mm, "end": v(242, -6.28) * mm});
            skLineSegment(sketch, "E7.5.0.81", {"start": v(238, -9.55) * mm, "end": v(238, -11.55) * mm});
            skLineSegment(sketch, "E7.5.0.82", {"start": v(278, 6.27) * mm, "end": v(278, 4.27) * mm});
            skLineSegment(sketch, "E7.5.0.85", {"start": v(258, 1) * mm, "end": v(262, 1) * mm});
            skLineSegment(sketch, "E7.5.0.86", {"start": v(248, 6.27) * mm, "end": v(248, 4.27) * mm});
            skLineSegment(sketch, "E7.5.0.87", {"start": v(242, -9.55) * mm, "end": v(242, -11.55) * mm});
            skLineSegment(sketch, "E7.5.0.89", {"start": v(282, 11.55) * mm, "end": v(282, 9.55) * mm});
            skLineSegment(sketch, "E7.5.0.90", {"start": v(272, -4.28) * mm, "end": v(272, -6.28) * mm});
            skLineSegment(sketch, "E7.5.0.93", {"start": v(258, 4.27) * mm, "end": v(262, 4.27) * mm});
            skLineSegment(sketch, "E7.5.0.94", {"start": v(248, 11.55) * mm, "end": v(248, 9.55) * mm});
            skLineSegment(sketch, "E7.5.0.95", {"start": v(238, -4.28) * mm, "end": v(242, -4.28) * mm});
            skLineSegment(sketch, "E7.5.0.96", {"start": v(278, 9.55) * mm, "end": v(282, 9.55) * mm});
            skLineSegment(sketch, "E7.5.0.99", {"start": v(252, 11.55) * mm, "end": v(252, 9.55) * mm});
            skLineSegment(sketch, "E7.5.0.100", {"start": v(238, -9.55) * mm, "end": v(242, -9.55) * mm});
            skLineSegment(sketch, "E7.5.0.102", {"start": v(278, 11.55) * mm, "end": v(278, 9.55) * mm});
            skLineSegment(sketch, "E7.5.0.103", {"start": v(268, -4.28) * mm, "end": v(272, -4.28) * mm});
            skLineSegment(sketch, "E7.5.0.106", {"start": v(228, 4.27) * mm, "end": v(232, 4.27) * mm});
            skLineSegment(sketch, "E7.5.0.107", {"start": v(262, 6.27) * mm, "end": v(262, 4.27) * mm});
            skLineSegment(sketch, "E7.5.0.108", {"start": v(248, 9.55) * mm, "end": v(252, 9.55) * mm});
            skLineSegment(sketch, "E7.5.0.109", {"start": v(238, -4.28) * mm, "end": v(238, -6.28) * mm});
            skLineSegment(sketch, "E7.5.0.112", {"start": v(278, -6.28) * mm, "end": v(282, -6.28) * mm});
            skLineSegment(sketch, "E7.5.0.114", {"start": v(238, -11.55) * mm, "end": v(242, -11.55) * mm});
            skLineSegment(sketch, "E7.5.0.115", {"start": v(232, 6.27) * mm, "end": v(232, 4.27) * mm});
            skLineSegment(sketch, "E7.5.0.116", {"start": v(258, 6.27) * mm, "end": v(262, 6.27) * mm});
            skLineSegment(sketch, "E7.5.0.117", {"start": v(248, -6.28) * mm, "end": v(252, -6.28) * mm});
            skLineSegment(sketch, "E7.5.0.120", {"start": v(278, 11.55) * mm, "end": v(282, 11.55) * mm});
            skLineSegment(sketch, "E7.5.0.122", {"start": v(242, 1) * mm, "end": v(242, -1) * mm});
            skLineSegment(sketch, "E7.5.0.123", {"start": v(228, 6.27) * mm, "end": v(232, 6.27) * mm});
            skLineSegment(sketch, "E7.5.0.124", {"start": v(218, -6.28) * mm, "end": v(222, -6.28) * mm});
            skLineSegment(sketch, "E7.5.0.125", {"start": v(258, 6.27) * mm, "end": v(258, 4.27) * mm});
            skLineSegment(sketch, "E7.5.0.126", {"start": v(248, 11.55) * mm, "end": v(252, 11.55) * mm});
            skLineSegment(sketch, "E7.5.0.129", {"start": v(282, -4.28) * mm, "end": v(282, -6.28) * mm});
            skLineSegment(sketch, "E7.5.0.132", {"start": v(268, 1) * mm, "end": v(268, -1) * mm});
            skLineSegment(sketch, "E7.5.0.133", {"start": v(262, 11.55) * mm, "end": v(262, 9.55) * mm});
            skLineSegment(sketch, "E7.5.0.134", {"start": v(252, -4.28) * mm, "end": v(252, -6.28) * mm});
            skLineSegment(sketch, "E7.5.0.135", {"start": v(278, -4.28) * mm, "end": v(282, -4.28) * mm});
            skLineSegment(sketch, "E7.5.0.136", {"start": v(282, 9.55) * mm, "end": v(282, 4.27) * mm, "construction": true});
            skLineSegment(sketch, "E7.5.0.138", {"start": v(238, 1) * mm, "end": v(242, 1) * mm});
            skLineSegment(sketch, "E7.5.0.139", {"start": v(218, -9.55) * mm, "end": v(218, -11.55) * mm});
            skLineSegment(sketch, "E7.5.0.140", {"start": v(278, -4.28) * mm, "end": v(278, -6.28) * mm});
            skLineSegment(sketch, "E7.5.0.141", {"start": v(218, -11.55) * mm, "end": v(228, -11.55) * mm, "construction": true});
            skLineSegment(sketch, "E7.5.0.142", {"start": v(232, 11.55) * mm, "end": v(232, 9.55) * mm});
            skLineSegment(sketch, "E7.5.0.143", {"start": v(218, -9.55) * mm, "end": v(222, -9.55) * mm});
            skLineSegment(sketch, "E7.5.0.144", {"start": v(258, 11.55) * mm, "end": v(258, 9.55) * mm});
            skLineSegment(sketch, "E7.5.0.145", {"start": v(248, -4.28) * mm, "end": v(252, -4.28) * mm});
            skLineSegment(sketch, "E7.5.0.146", {"start": v(252, 9.55) * mm, "end": v(252, 4.27) * mm, "construction": true});
            skLineSegment(sketch, "E7.5.0.147", {"start": v(238, 4.27) * mm, "end": v(242, 4.27) * mm});
            skLineSegment(sketch, "E7.5.0.148", {"start": v(228, 11.55) * mm, "end": v(228, 9.55) * mm});
            skLineSegment(sketch, "E7.5.0.149", {"start": v(222, -9.55) * mm, "end": v(222, -11.55) * mm});
            skLineSegment(sketch, "E7.5.0.150", {"start": v(258, 9.55) * mm, "end": v(262, 9.55) * mm});
            skLineSegment(sketch, "E7.5.0.151", {"start": v(248, -4.28) * mm, "end": v(248, -6.28) * mm});
            skLineSegment(sketch, "E7.5.0.152", {"start": v(248, -1) * mm, "end": v(252, -1) * mm});
            skLineSegment(sketch, "E7.5.0.155", {"start": v(218, -4.28) * mm, "end": v(218, -6.28) * mm});
            skLineSegment(sketch, "E7.5.0.156", {"start": v(218, -4.28) * mm, "end": v(222, -4.28) * mm});
            skLineSegment(sketch, "E7.5.0.157", {"start": v(222, -4.28) * mm, "end": v(222, -6.28) * mm});
            skLineSegment(sketch, "E7.5.0.158", {"start": v(222, 6.27) * mm, "end": v(222, 4.27) * mm});
            skLineSegment(sketch, "E7.5.0.159", {"start": v(218, 1) * mm, "end": v(218, -1) * mm});
            skLineSegment(sketch, "E7.5.0.160", {"start": v(218, 1) * mm, "end": v(222, 1) * mm});
            skLineSegment(sketch, "E7.5.0.161", {"start": v(228, 9.55) * mm, "end": v(232, 9.55) * mm});
            skLineSegment(sketch, "E7.5.0.162", {"start": v(218, -11.55) * mm, "end": v(222, -11.55) * mm});
            skLineSegment(sketch, "E7.5.0.163", {"start": v(218, -1) * mm, "end": v(222, -1) * mm});
            skLineSegment(sketch, "E7.5.0.164", {"start": v(258, -6.28) * mm, "end": v(262, -6.28) * mm});
            skLineSegment(sketch, "E7.5.0.165", {"start": v(258, -9.55) * mm, "end": v(258, -11.55) * mm});
            skLineSegment(sketch, "E7.5.0.167", {"start": v(238, 6.27) * mm, "end": v(242, 6.27) * mm});
            skLineSegment(sketch, "E7.5.0.168", {"start": v(228, -6.28) * mm, "end": v(232, -6.28) * mm});
            skLineSegment(sketch, "E7.5.0.169", {"start": v(228, -9.55) * mm, "end": v(228, -11.55) * mm});
            skLineSegment(sketch, "E7.5.0.170", {"start": v(258, 11.55) * mm, "end": v(262, 11.55) * mm});
            skLineSegment(sketch, "E7.5.0.171", {"start": v(262, -9.55) * mm, "end": v(262, -11.55) * mm});
            skLineSegment(sketch, "E7.5.0.172", {"start": v(252, 1) * mm, "end": v(252, -1) * mm});
            skLineSegment(sketch, "E7.5.0.175", {"start": v(278, 1) * mm, "end": v(278, -1) * mm});
            skLineSegment(sketch, "E7.5.0.176", {"start": v(258, -4.28) * mm, "end": v(258, -6.28) * mm});
            skLineSegment(sketch, "E7.5.0.177", {"start": v(228, -1) * mm, "end": v(232, -1) * mm});
            skLineSegment(sketch, "E7.5.0.178", {"start": v(228, -4.28) * mm, "end": v(228, -6.28) * mm});
            skLineSegment(sketch, "E7.5.0.179", {"start": v(232, 1) * mm, "end": v(232, -1) * mm});
            skLineSegment(sketch, "E7.5.0.181", {"start": v(242, 9.55) * mm, "end": v(242, 4.27) * mm, "construction": true});
            skLineSegment(sketch, "E7.5.0.182", {"start": v(228, 1) * mm, "end": v(228, -1) * mm});
            skLineSegment(sketch, "E7.5.0.184", {"start": v(268, -4.28) * mm, "end": v(268, -6.28) * mm});
            skLineSegment(sketch, "E7.5.0.185", {"start": v(228, 1) * mm, "end": v(232, 1) * mm});
            skLineSegment(sketch, "E7.5.0.186", {"start": v(258, 1) * mm, "end": v(258, -1) * mm});
            skLineSegment(sketch, "E7.5.0.187", {"start": v(242, -4.28) * mm, "end": v(242, -6.28) * mm});
            skLineSegment(sketch, "E7.5.0.188", {"start": v(272, 9.55) * mm, "end": v(272, 4.27) * mm, "construction": true});
            skLineSegment(sketch, "E7.5.0.193", {"start": v(278, -1) * mm, "end": v(282, -1) * mm});
            skLineSegment(sketch, "E7.5.0.194", {"start": v(268, 4.27) * mm, "end": v(272, 4.27) * mm});
            skLineSegment(sketch, "E7.5.0.196", {"start": v(272, 6.27) * mm, "end": v(272, 4.27) * mm});
            skLineSegment(sketch, "E7.5.0.198", {"start": v(222, 11.55) * mm, "end": v(222, 9.55) * mm});
            skLineSegment(sketch, "E7.5.0.199", {"start": v(222, 1) * mm, "end": v(222, -1) * mm});
            skLineSegment(sketch, "E7.5.0.200", {"start": v(242, 6.27) * mm, "end": v(242, 4.27) * mm});
            skLineSegment(sketch, "E7.5.0.201", {"start": v(268, 6.27) * mm, "end": v(272, 6.27) * mm});
            skLineSegment(sketch, "E7.5.0.202", {"start": v(222, 9.55) * mm, "end": v(222, 4.27) * mm, "construction": true});
            skLineSegment(sketch, "E7.5.0.204", {"start": v(282, 1) * mm, "end": v(282, -1) * mm});
            skLineSegment(sketch, "E7.5.0.206", {"start": v(268, 6.27) * mm, "end": v(268, 4.27) * mm});
            skLineSegment(sketch, "E7.5.0.209", {"start": v(278, 1) * mm, "end": v(282, 1) * mm});
            skLineSegment(sketch, "E7.direction1", {"start": v(-272, -9.55) * mm, "end": v(-172, -9.55) * mm, "construction": true});
            skSolve(sketch);
        }
        {
            var Q0;
            Q0=qSketchRegion(id+"F2",true);
            extrude(context, id + "F3", {"entities" : qUnion([Q0]), "operationType" : NewBodyOperationType.ADD, "depth" : 1 * mm});
        }
        {
            var Q0;
            Q0=makeQuery(id+"F1.opExtrude","SWEPT_BODY",BODY,{"disambiguationData":[OSD([sQuery(id+"F0.wireOp",EDGE,"E0"),sQuery(id+"F0.wireOp",EDGE,"E1")])]});
            transform(context, id + "F4", {"entities" : qUnion([Q0]), "transformType" : TransformType.TRANSLATION_3D, "dx" : 0 * mm, "dy" : 0 * mm, "dz" : 0 * mm, "makeCopy" : true});
        }
    });
